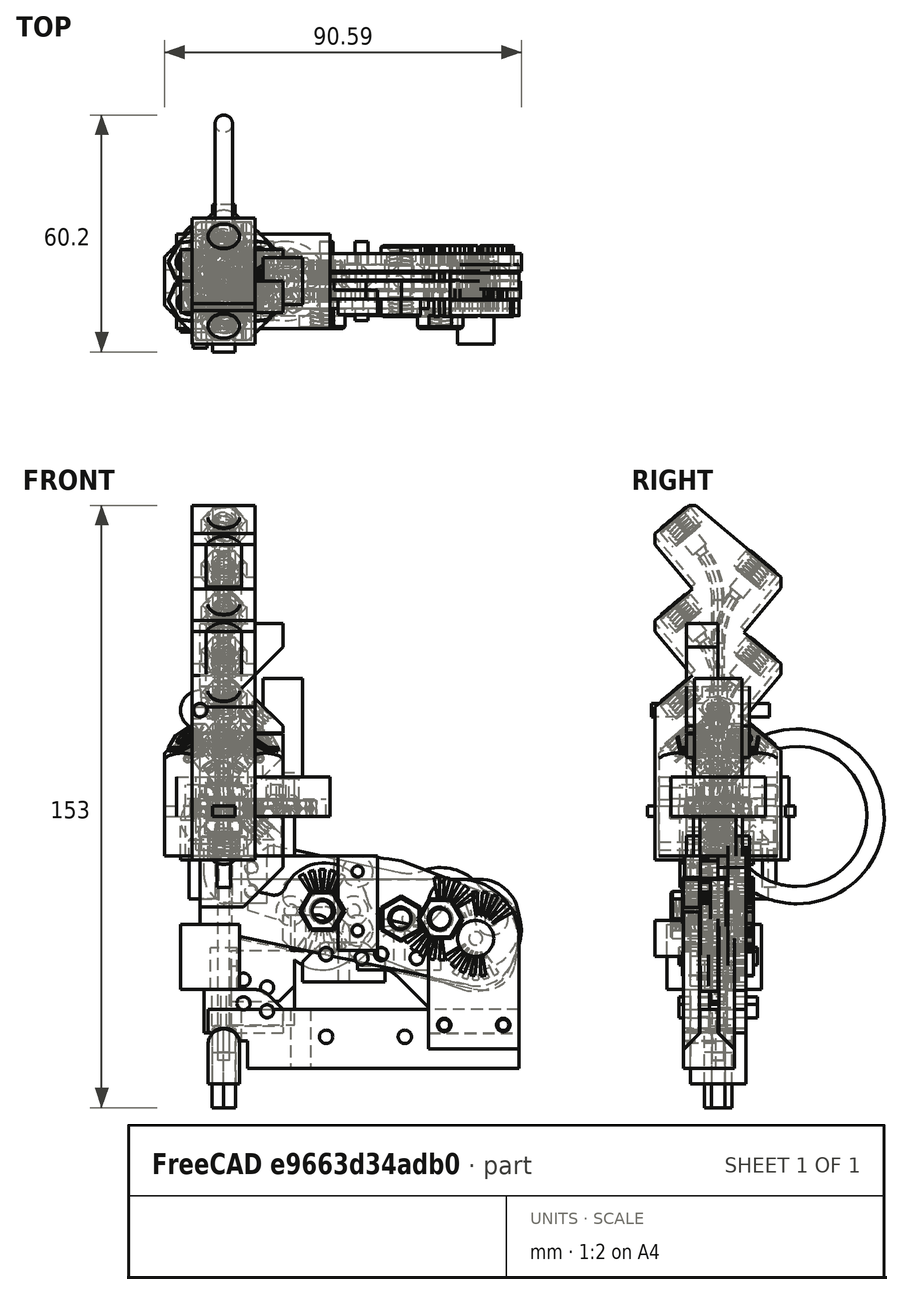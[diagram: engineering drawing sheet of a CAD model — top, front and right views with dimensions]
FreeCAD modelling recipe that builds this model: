
FCSTD DOCUMENT  (FreeCAD 0.17R13528 (Git))
Label: guillotine-old
License: All rights reserved
LicenseURL: http://en.wikipedia.org/wiki/All_rights_reserved
objects: Part::Cylinder×189, Part::Box×143, Part::Cut×137, Part::MultiFuse×132, Part::MultiCommon×72, Part::Feature×58, Part::Cone×39, Part::Fillet×29, Part::Chamfer×26, Part::Mirroring×13, Part::Torus×9, App::DocumentObjectGroup×5, Part::Fuse×2, Part::Sphere×1
note: 850 computed .brp shape members not serialized (recipe doc carries the construction recipe); baked Part::Feature solids carry a one-line shape summary decoded from their .brp

FEATURE [Part::Feature] Part__Feature027  label="1310"
  Placement = pos=(2,0,0) rot=(0,0,1;0rad)
  shape: bbox 13.32 x 18 x 18 mm, 178 faces (baked)
FEATURE [Part::Box] Box  label="Cube"
  AttacherType = Attacher::AttachEngine3D
  Height = 20
  Length = 4
  Placement = pos=(0,-10,-10) rot=(0,0,1;0rad)
  Width = 20
FEATURE [Part::Cylinder] Cylinder
  Angle = 360
  AttacherType = Attacher::AttachEngine3D
  Height = 25
  Placement = pos=(-4,0,0) rot=(0,1,0;1.5708rad)
  Radius = 5
FEATURE [Part::MultiFuse] Fusion
  Shapes = -> [Part__Feature027,Cylinder]
FEATURE [Part::MultiCommon] Common  label="gear-blank"
  Shapes = -> [Fusion,Box]
FEATURE [Part::Cylinder] Cylinder001
  Angle = 360
  AttacherType = Attacher::AttachEngine3D
  Height = 10
  Placement = pos=(-2,0,0) rot=(0,1,0;1.5708rad)
  Radius = 1.7
FEATURE [Part::Feature] Part__Feature028  label="1310001"
  Placement = pos=(2,0,0) rot=(0,0,1;0rad)
  shape: bbox 13.32 x 18 x 18 mm, 178 faces (baked)
FEATURE [Part::Box] Box001  label="Cube001"
  AttacherType = Attacher::AttachEngine3D
  Height = 20
  Length = 4
  Placement = pos=(0,-10,-10) rot=(0,0,1;0rad)
  Width = 20
FEATURE [Part::Cylinder] Cylinder002
  Angle = 360
  AttacherType = Attacher::AttachEngine3D
  Height = 25
  Placement = pos=(-4,0,0) rot=(0,1,0;1.5708rad)
  Radius = 5
FEATURE [Part::MultiFuse] Fusion001
  Shapes = -> [Part__Feature028,Cylinder002]
FEATURE [Part::MultiCommon] Common001  label="gear-blank001"
  Shapes = -> [Fusion001,Box001]
FEATURE [Part::Cylinder] Cylinder003
  Angle = 360
  AttacherType = Attacher::AttachEngine3D
  Height = 10
  Placement = pos=(-2,0,0) rot=(0,1,0;1.5708rad)
  Radius = 1.8
FEATURE [Part::Cut] Cut  label="shaft-gear-a"
  Base = -> Common
  Placement = pos=(0,0,0) rot=(0,-1,0;1.5708rad)
  Tool = -> Cylinder001
FEATURE [Part::Box] Box002  label="Cube002"
  AttacherType = Attacher::AttachEngine3D
  Height = 10
  Length = 15
  Placement = pos=(-4,-6,1) rot=(0,0,1;0rad)
  Width = 10
FEATURE [Part::Cut] Cut001
  Base = -> Cylinder003
  Tool = -> Box002
FEATURE [Part::Cut] Cut002  label="motor-gear"
  Base = -> Common001
  Placement = pos=(15,0,4) rot=(0,1,0;1.5708rad)
  Tool = -> Cut001
FEATURE [Part::Fuse] Fusion003
FEATURE [Part::Cylinder] Cylinder012
  Angle = 360
  AttacherType = Attacher::AttachEngine3D
  Height = 10
  Placement = pos=(5,-4.5,0) rot=(0,1,0;1.5708rad)
  Radius = 0.8
FEATURE [Part::Fuse] Fusion048  label="motor"
  Base = -> Cylinder012
  Placement = pos=(15,0,0) rot=(0,-1,0;1.5708rad)
  Tool = -> Fusion003
FEATURE [Part::Feature] Part__Feature035  label="423001001"
  Placement = pos=(0,0,-2) rot=(0,0,1;3.74342rad)
  shape: bbox 9 x 9 x 4 mm, 22 faces (baked)
FEATURE [Part::Feature] Part__Feature066  label="212001001001"
  Placement = pos=(0,0,0) rot=(0.905883,0.423527,0;3.14159rad)
  shape: bbox 7 x 7 x 0.5 mm, 6 faces (baked)
FEATURE [Part::Cylinder] Cylinder013
  Angle = 360
  AttacherType = Attacher::AttachEngine3D
  Height = 74
  Placement = pos=(0,0,-62) rot=(0,0,1;0rad)
  Radius = 1.5
FEATURE [Part::Cylinder] Cylinder014
  Angle = 360
  AttacherType = Attacher::AttachEngine3D
  Height = 8
  Placement = pos=(0,0,1) rot=(0,0,1;0rad)
  Radius = 4
FEATURE [Part::Box] Box003  label="Cube003"
  AttacherType = Attacher::AttachEngine3D
  Height = 10
  Length = 10
  Placement = pos=(-12.85,-5,0) rot=(0,0,1;0rad)
  Width = 10
FEATURE [Part::Feature] Box001001
  Placement = pos=(-2.09487,-13.6284,0) rot=(0,0,1;1.0472rad)
  shape: bbox 13.66 x 13.66 x 10 mm, 6 faces (baked)
FEATURE [Part::Feature] Box001002
  Placement = pos=(10.7551,-8.62843,0) rot=(0,0,1;2.0944rad)
  shape: bbox 13.66 x 13.66 x 10 mm, 6 faces (baked)
FEATURE [Part::Feature] Box001003
  Placement = pos=(12.85,5,0) rot=(0,0,1;3.14159rad)
  shape: bbox 10 x 10 x 10 mm, 6 faces (baked)
FEATURE [Part::Feature] Box001004
  Placement = pos=(2.09487,13.6284,0) rot=(0,0,1;4.18879rad)
  shape: bbox 13.66 x 13.66 x 10 mm, 6 faces (baked)
FEATURE [Part::Feature] Box001005
  Placement = pos=(-10.7551,8.62843,0) rot=(0,0,-1;1.0472rad)
  shape: bbox 13.66 x 13.66 x 10 mm, 6 faces (baked)
FEATURE [Part::MultiFuse] Fusion049
  Shapes = -> [Box003,Box001005,Box001001,Box001002,Box001003,Box001004]
FEATURE [Part::Cut] Cut003  label="m3-nut"
  Base = -> Cylinder014
  Placement = pos=(0,0,1) rot=(0,0,1;0rad)
  Tool = -> Fusion049
FEATURE [Part::Feature] Part__Feature067  label="423001001001"
  Placement = pos=(0,0,7) rot=(0,0,1;3.74342rad)
  shape: bbox 9 x 9 x 4 mm, 22 faces (baked)
FEATURE [Part::Cylinder] Cylinder015
  Angle = 360
  AttacherType = Attacher::AttachEngine3D
  Height = 100
  Placement = pos=(0,0,-12) rot=(0,0,1;0rad)
  Radius = 1.7
FEATURE [Part::MultiFuse] Fusion050
  Shapes = -> [Cylinder015,Cut003]
FEATURE [Part::Cut] Cut004  label="shaft-gear"
  Base = -> Cut
  Tool = -> Fusion050
FEATURE [Part::Box] Box001006  label="Cube004"
  AttacherType = Attacher::AttachEngine3D
  Height = 10
  Length = 39
  Placement = pos=(-12,-12,0) rot=(0,0,1;0rad)
  Width = 24
FEATURE [Part::Cylinder] Cylinder016
  Angle = 360
  AttacherType = Attacher::AttachEngine3D
  Height = 30
  Placement = pos=(0,0,-12) rot=(0,0,1;0rad)
  Radius = 3.5
FEATURE [Part::Cylinder] Cylinder017
  Angle = 360
  AttacherType = Attacher::AttachEngine3D
  Height = 30
  Placement = pos=(0,0,-21.5) rot=(0,0,1;0rad)
  Radius = 4.7
FEATURE [Part::Cylinder] Cylinder018
  Angle = 360
  AttacherType = Attacher::AttachEngine3D
  Height = 30
  Placement = pos=(0,0,-25.5) rot=(0,0,1;0rad)
  Radius = 10
FEATURE [Part::Cylinder] Cylinder019
  Angle = 360
  AttacherType = Attacher::AttachEngine3D
  Height = 30
  Placement = pos=(16,0,-25.5) rot=(0,0,1;0rad)
  Radius = 10
FEATURE [Part::Cylinder] Cylinder020
  Angle = 360
  AttacherType = Attacher::AttachEngine3D
  Height = 30
  Placement = pos=(17,0,-12.5) rot=(0,0,1;0rad)
  Radius = 2.1
FEATURE [Part::Cylinder] Cylinder021
  Angle = 360
  AttacherType = Attacher::AttachEngine3D
  Height = 30
  Placement = pos=(17,-4.5,-12.5) rot=(0,0,1;0rad)
  Radius = 1
FEATURE [Part::Cylinder] Cylinder022
  Angle = 360
  AttacherType = Attacher::AttachEngine3D
  Height = 30
  Placement = pos=(17,4.5,-12.5) rot=(0,0,1;0rad)
  Radius = 1
FEATURE [Part::Cylinder] Cylinder023
  Angle = 360
  AttacherType = Attacher::AttachEngine3D
  Height = 30
  Placement = pos=(13,0,-12.5) rot=(0,0,1;0rad)
  Radius = 2.1
FEATURE [Part::Cylinder] Cylinder024
  Angle = 360
  AttacherType = Attacher::AttachEngine3D
  Height = 30
  Placement = pos=(13,-4.5,-12.5) rot=(0,0,1;0rad)
  Radius = 1
FEATURE [Part::Cylinder] Cylinder025
  Angle = 360
  AttacherType = Attacher::AttachEngine3D
  Height = 30
  Placement = pos=(13,4.5,-12.5) rot=(0,0,1;0rad)
  Radius = 1
FEATURE [Part::Box] Box001007  label="Cube005"
  AttacherType = Attacher::AttachEngine3D
  Height = 27
  Length = 4
  Placement = pos=(13,-2.1,-11) rot=(0,0,1;0rad)
  Width = 4.2
FEATURE [Part::Box] Box001008  label="Cube006"
  AttacherType = Attacher::AttachEngine3D
  Height = 27
  Length = 4
  Placement = pos=(13,-5.5,-11) rot=(0,0,1;0rad)
  Width = 2
FEATURE [Part::Box] Box001009  label="Cube007"
  AttacherType = Attacher::AttachEngine3D
  Height = 27
  Length = 4
  Placement = pos=(13,3.5,-11) rot=(0,0,1;0rad)
  Width = 2
FEATURE [Part::MultiFuse] Fusion052  label="motor-slots"
  Shapes = -> [Box001009,Cylinder021,Cylinder022,Box001007,Cylinder020,Cylinder023,Cylinder024,Box001008,Cylinder025]
FEATURE [Part::Cylinder] Cylinder026
  Angle = 360
  AttacherType = Attacher::AttachEngine3D
  Height = 30
  Placement = pos=(15,0,-25.5) rot=(0,0,1;0rad)
  Radius = 10
FEATURE [Part::MultiFuse] Fusion053  label="gearbox-cavity-1"
  Shapes = -> [Cylinder019,Cylinder016,Cylinder017,Cylinder018,Cylinder026]
FEATURE [Part::MultiFuse] Fusion054  label="gearbox-cavity-2"
  Shapes = -> [Fusion053,Fusion052]
FEATURE [Part::Cut] Cut005  label="gearbox-1"
  Base = -> Box001006
  Tool = -> Fusion054
FEATURE [Part::Chamfer] Chamfer  label="gearbox-2"
  Base = -> Cut005
  Edges = 10 edges r=1: [Edge47,Edge50,Edge52,Edge54,Edge55,Edge58,Edge60,Edge62,Edge64,Edge65]
FEATURE [Part::Box] Box001010  label="Cube008"
  AttacherType = Attacher::AttachEngine3D
  Height = 8
  Length = 14
  Placement = pos=(-7,-15,-8.5) rot=(0,0,1;0rad)
  Width = 30
FEATURE [Part::Box] Box001011  label="Cube009"
  AttacherType = Attacher::AttachEngine3D
  Height = 11
  Length = 14
  Placement = pos=(-7,-15,-1) rot=(0,0,1;0rad)
  Width = 2.8
FEATURE [Part::Box] Box001012  label="Cube010"
  AttacherType = Attacher::AttachEngine3D
  Height = 11
  Length = 14
  Placement = pos=(-7,12.2,-1) rot=(0,0,1;0rad)
  Width = 2.8
FEATURE [Part::MultiFuse] Fusion055  label="bearing-clamp-1"
  Shapes = -> [Box001010,Box001012,Box001011]
FEATURE [Part::Cylinder] Cylinder027  label="M3-tap-1"
  Angle = 360
  AttacherType = Attacher::AttachEngine3D
  Height = 19
  Placement = pos=(-4,24,6) rot=(1,0,0;1.5708rad)
  Radius = 1.4
FEATURE [Part::Cylinder] Cylinder028  label="M3-tap-2"
  Angle = 360
  AttacherType = Attacher::AttachEngine3D
  Height = 19
  Placement = pos=(4,24,6) rot=(1,0,0;1.5708rad)
  Radius = 1.4
FEATURE [Part::Cylinder] Cylinder029  label="M3-clear-1"
  Angle = 360
  AttacherType = Attacher::AttachEngine3D
  Height = 19
  Placement = pos=(-4,24,6) rot=(1,0,0;1.5708rad)
  Radius = 1.7
FEATURE [Part::Cylinder] Cylinder030  label="M3-clear-2"
  Angle = 360
  AttacherType = Attacher::AttachEngine3D
  Height = 19
  Placement = pos=(4,24,6) rot=(1,0,0;1.5708rad)
  Radius = 1.7
FEATURE [Part::Cylinder] Cylinder031  label="M3-tap-003"
  Angle = 360
  AttacherType = Attacher::AttachEngine3D
  Height = 19
  Placement = pos=(-4,24,6) rot=(1,0,0;1.5708rad)
  Radius = 1.4
FEATURE [Part::Cylinder] Cylinder032  label="M3-tap-004"
  Angle = 360
  AttacherType = Attacher::AttachEngine3D
  Height = 19
  Placement = pos=(4,24,6) rot=(1,0,0;1.5708rad)
  Radius = 1.4
FEATURE [Part::Cylinder] Cylinder033  label="M3-clear-003"
  Angle = 360
  AttacherType = Attacher::AttachEngine3D
  Height = 19
  Placement = pos=(4,24,6) rot=(1,0,0;1.5708rad)
  Radius = 1.7
FEATURE [Part::Cylinder] Cylinder034  label="M3-clear-004"
  Angle = 360
  AttacherType = Attacher::AttachEngine3D
  Height = 19
  Placement = pos=(-4,24,6) rot=(1,0,0;1.5708rad)
  Radius = 1.7
FEATURE [Part::Mirroring] Part__Mirroring  label="M3-tap-003 (Mirror #1)"
  Base = (0,0,0)
  Normal = (0,1,0)
  Source = -> Cylinder031
FEATURE [Part::Mirroring] Part__Mirroring001  label="M3-tap-004 (Mirror #2)"
  Base = (0,0,0)
  Normal = (0,1,0)
  Source = -> Cylinder032
FEATURE [Part::Mirroring] Part__Mirroring002  label="M3-clear-003 (Mirror #3)"
  Base = (0,0,0)
  Normal = (0,1,0)
  Source = -> Cylinder033
FEATURE [Part::Mirroring] Part__Mirroring003  label="M3-clear-004 (Mirror #4)"
  Base = (0,0,0)
  Normal = (0,1,0)
  Source = -> Cylinder034
FEATURE [Part::MultiFuse] Fusion056  label="M3-tap-a"
  Shapes = -> [Cylinder027,Cylinder028,Part__Mirroring,Part__Mirroring001]
FEATURE [Part::MultiFuse] Fusion057  label="M3-clear-a"
  Shapes = -> [Cylinder029,Cylinder030,Part__Mirroring002,Part__Mirroring003]
FEATURE [Part::Cut] Cut006  label="bearing-clamp-2"
  Base = -> Fusion055
  Tool = -> Fusion057
FEATURE [Part::Cut] Cut007  label="gearbox-3"
  Base = -> Chamfer
  Tool = -> Fusion056
FEATURE [Part::Cylinder] Cylinder035
  Angle = 360
  AttacherType = Attacher::AttachEngine3D
  Height = 30
  Placement = pos=(0,0,-4.5) rot=(0,0,1;0rad)
  Radius = 4.7
FEATURE [Part::Cylinder] Cylinder036
  Angle = 360
  AttacherType = Attacher::AttachEngine3D
  Height = 30
  Placement = pos=(0,0,-9) rot=(0,0,1;0rad)
  Radius = 3.5
FEATURE [Part::Box] Box001013  label="Cube011"
  AttacherType = Attacher::AttachEngine3D
  Height = 12
  Length = 80
  Placement = pos=(0,-2,0) rot=(0,0,1;0rad)
  Width = 4
FEATURE [Part::Cylinder] Cylinder037
  Angle = 360
  AttacherType = Attacher::AttachEngine3D
  Height = 4
  Placement = pos=(11,2,12) rot=(1,0,0;1.5708rad)
  Radius = 11
FEATURE [Part::Cylinder] Cylinder038
  Angle = 360
  AttacherType = Attacher::AttachEngine3D
  Height = 4
  Placement = pos=(50,2,12) rot=(1,0,0;1.5708rad)
  Radius = 11
FEATURE [Part::MultiFuse] Fusion059
  Shapes = -> [Box001013,Cylinder037,Cylinder038]
FEATURE [Part::Fillet] Fillet
  Base = -> Fusion059
  Edges = 1 edges r=7: [Edge21]
FEATURE [Part::Fillet] Fillet001
  Base = -> Fillet
  Edges = 2 edges r=7: [Edge12,Edge20]
FEATURE [Part::Cylinder] Cylinder039
  Angle = 360
  AttacherType = Attacher::AttachEngine3D
  Height = 10
  Placement = pos=(50,5,8) rot=(1,0,0;1.5708rad)
  Radius = 3.2
FEATURE [Part::Cut] Cut009
  Base = -> Fillet001
  Tool = -> Cylinder039
FEATURE [Part::Box] Box001014  label="Cube012"
  AttacherType = Attacher::AttachEngine3D
  Height = 13
  Length = 2
  Placement = pos=(0,-5,0) rot=(0,0,1;0rad)
  Width = 10
FEATURE [Part::Box] Box001015  label="Cube013"
  AttacherType = Attacher::AttachEngine3D
  Height = 2
  Length = 13
  Placement = pos=(0,-5,0) rot=(0,-1,0;1.39626rad)
  Width = 10
FEATURE [Part::Cylinder] Cylinder040
  Angle = 360
  AttacherType = Attacher::AttachEngine3D
  Height = 13
  Placement = pos=(0,7,0) rot=(1,0,0;1.5708rad)
  Radius = 2
FEATURE [Part::Cylinder] Cylinder041
  Angle = 360
  AttacherType = Attacher::AttachEngine3D
  Height = 8
  Placement = pos=(0,4,0) rot=(1,0,0;1.5708rad)
  Radius = 8
FEATURE [Part::Cut] Cut010
  Base = -> Cylinder041
  Tool = -> Cylinder040
FEATURE [Part::MultiCommon] Common002
  Shapes = -> [Box001014,Box001015]
FEATURE [Part::MultiCommon] Common003
  Placement = pos=(50,0,11) rot=(0,-1,0;0.087266rad)
  Shapes = -> [Cut010,Common002]
FEATURE [Part::MultiCommon] Common004
  Placement = pos=(50.7765,0,10.8978) rot=(0,1,0;0.174533rad)
  Shapes = -> [Cut010,Common002]
FEATURE [Part::MultiCommon] Common005
  Placement = pos=(49.2235,0,10.8978) rot=(0,-1,0;0.349066rad)
  Shapes = -> [Cut010,Common002]
FEATURE [Part::MultiCommon] Common006
  Placement = pos=(51.5,0,10.5981) rot=(0,1,0;0.436332rad)
  Shapes = -> [Cut010,Common002]
FEATURE [Part::MultiCommon] Common007
  Placement = pos=(48.5,0,10.5981) rot=(0,-1,0;0.610865rad)
  Shapes = -> [Cut010,Common002]
FEATURE [Part::MultiFuse] Fusion060  label="strength-slots"
  Shapes = -> [Common003,Common006,Common005,Common004,Common007]
FEATURE [Part::MultiFuse] Fusion061  label="strength-slots001"
  Placement = pos=(61,0,22) rot=(0,1,0;3.14159rad)
  Shapes = -> [Common003,Common006,Common005,Common004,Common007]
FEATURE [Part::Cut] Cut011
  Base = -> Cut009
  Tool = -> Fusion060
FEATURE [Part::Cylinder] Cylinder042
  Angle = 360
  AttacherType = Attacher::AttachEngine3D
  Height = 10
  Placement = pos=(11,5,15) rot=(1,0,0;1.5708rad)
  Radius = 4.6
FEATURE [Part::Cut] Cut012
  Base = -> Cut011
  Tool = -> Cylinder042
FEATURE [Part::Cut] Cut013
  Base = -> Cut012
  Tool = -> Fusion061
FEATURE [Part::Fillet] Fillet002  label="cutting-lever-1"
  Base = -> Cut013
  Edges = 1 edges r=10: [Edge73]
  Placement = pos=(75,0,-16) rot=(0,1,0;3.14159rad)
FEATURE [Part::Box] Box001016  label="Cube014"
  AttacherType = Attacher::AttachEngine3D
  Height = 12
  Length = 80
  Placement = pos=(0,-7,12) rot=(0,0,1;0rad)
  Width = 14
FEATURE [Part::Cylinder] Cylinder043
  Angle = 360
  AttacherType = Attacher::AttachEngine3D
  Height = 14
  Placement = pos=(11,7,12) rot=(1,0,0;1.5708rad)
  Radius = 11
FEATURE [Part::Cylinder] Cylinder044
  Angle = 360
  AttacherType = Attacher::AttachEngine3D
  Height = 14
  Placement = pos=(50,7,12) rot=(1,0,0;1.5708rad)
  Radius = 11
FEATURE [Part::MultiFuse] Fusion062  label="cutting-holder-1"
  Shapes = -> [Cylinder044,Cylinder043,Box001016]
FEATURE [Part::Fillet] Fillet003
  Base = -> Fusion062
  Edges = 1 edges r=10: [Edge1]
  Placement = pos=(-1.94863,0,5.46002) rot=(0,1,0;0.20944rad)
FEATURE [Part::Cylinder] Cylinder045
  Angle = 360
  AttacherType = Attacher::AttachEngine3D
  Height = 20
  Placement = pos=(11,10,15) rot=(1,0,0;1.5708rad)
  Radius = 1.7
FEATURE [Part::Cylinder] Cylinder046
  Angle = 360
  AttacherType = Attacher::AttachEngine3D
  Height = 20
  Placement = pos=(50,10,8) rot=(1,0,0;1.5708rad)
  Radius = 3.2
FEATURE [Part::Box] Box001017  label="Cube015"
  AttacherType = Attacher::AttachEngine3D
  Height = 2
  Length = 13
  Placement = pos=(0,-10,0) rot=(0,-1,0;1.39626rad)
  Width = 20
FEATURE [Part::Box] Box001018  label="Cube016"
  AttacherType = Attacher::AttachEngine3D
  Height = 13
  Length = 2
  Placement = pos=(0,-10,0) rot=(0,0,1;0rad)
  Width = 20
FEATURE [Part::Cylinder] Cylinder047
  Angle = 360
  AttacherType = Attacher::AttachEngine3D
  Height = 26
  Placement = pos=(0,12,0) rot=(1,0,0;1.5708rad)
  Radius = 2
FEATURE [Part::Cylinder] Cylinder048
  Angle = 360
  AttacherType = Attacher::AttachEngine3D
  Height = 18
  Placement = pos=(0,9,0) rot=(1,0,0;1.5708rad)
  Radius = 8
FEATURE [Part::Cut] Cut014
  Base = -> Cylinder048
  Tool = -> Cylinder047
FEATURE [Part::MultiCommon] Common012  label="strength-slot-005"
  Placement = pos=(0,0,2.5) rot=(0,-1,0;0.087266rad)
  Shapes = -> [Box001017,Box001018,Cut014]
FEATURE [Part::Box] Box001019  label="Cube017"
  AttacherType = Attacher::AttachEngine3D
  Height = 40
  Length = 100
  Placement = pos=(-2,-2.5,-8) rot=(0,0,1;0rad)
  Width = 22
FEATURE [Part::MultiCommon] Common013  label="strength-slot-006"
  Placement = pos=(0.647048,0,2.41481) rot=(0,1,0;0.174533rad)
  Shapes = -> [Box001017,Box001018,Cut014]
FEATURE [Part::MultiCommon] Common014  label="strength-slot-007"
  Placement = pos=(1.25,0,2.16506) rot=(0,1,0;0.436332rad)
  Shapes = -> [Box001017,Box001018,Cut014]
FEATURE [Part::MultiCommon] Common015  label="strength-slot-008"
  Placement = pos=(-0.647048,0,2.41481) rot=(0,-1,0;0.349066rad)
  Shapes = -> [Box001017,Box001018,Cut014]
FEATURE [Part::MultiCommon] Common016  label="strength-slot-009"
  Placement = pos=(-1.25,0,2.16506) rot=(0,-1,0;0.610865rad)
  Shapes = -> [Box001017,Box001018,Cut014]
FEATURE [Part::MultiFuse] Fusion063  label="strength-slots002"
  Placement = pos=(11,0,15) rot=(0,0,1;0rad)
  Shapes = -> [Common012,Common013,Common014,Common015,Common016]
FEATURE [Part::MultiFuse] Fusion064  label="strength-slots003"
  Placement = pos=(50,0,8) rot=(0,1,0;3.14159rad)
  Shapes = -> [Common012,Common013,Common014,Common015,Common016]
FEATURE [Part::MultiFuse] Fusion065
  Shapes = -> [Cylinder045,Cylinder046,Fusion063,Fusion064]
FEATURE [Part::Box] Box001020  label="Cube018"
  AttacherType = Attacher::AttachEngine3D
  Height = 10
  Length = 21
  Placement = pos=(20,-2.5,13) rot=(0,0,1;0rad)
  Width = 9.5
FEATURE [Part::Chamfer] Chamfer001
  Base = -> Box001020
  Edges = 2 edges r=8: [Edge4,Edge8]
FEATURE [Part::Fillet] Fillet004
  Base = -> Chamfer001
  Edges = 2 edges r=2: [Edge10,Edge17]
FEATURE [Part::Fillet] Fillet005
  Base = -> Fillet003
  Edges = 1 edges r=7: [Edge26]
FEATURE [Part::Fillet] Fillet006
  Base = -> Fillet005
  Edges = 1 edges r=7: [Edge11]
FEATURE [Part::Cut] Cut015
  Base = -> Fillet006
  Tool = -> Fusion065
FEATURE [Part::Cut] Cut016  label="cutting-holder-2"
  Base = -> Cut015
  Tool = -> Box001019
FEATURE [Part::Cut] Cut017  label="cutting-holder-003"
  Base = -> Cut015
  Tool = -> Box001019
FEATURE [Part::Mirroring] Part__Mirroring004  label="cutting-holder-004"
  Base = (0,0,0)
  Normal = (0,1,0)
  Source = -> Cut017
FEATURE [Part::MultiFuse] Fusion066  label="cutting-holder-base"
  Shapes = -> [Fillet004,Part__Mirroring004]
FEATURE [Part::Cylinder] Cylinder049
  Angle = 360
  AttacherType = Attacher::AttachEngine3D
  Height = 30
  Placement = pos=(30.5,0,0) rot=(0,0,1;0rad)
  Radius = 1.4
FEATURE [Part::Cut] Cut018  label="cutting-holder-base-2"
  Base = -> Fusion066
  Tool = -> Cylinder049
FEATURE [Part::Cylinder] Cylinder050
  Angle = 360
  AttacherType = Attacher::AttachEngine3D
  Height = 20
  Placement = pos=(26,10,20) rot=(1,0,0;1.5708rad)
  Radius = 1.7
FEATURE [Part::Cylinder] Cylinder051
  Angle = 360
  AttacherType = Attacher::AttachEngine3D
  Height = 20
  Placement = pos=(35,10,19) rot=(1,0,0;1.5708rad)
  Radius = 1.7
FEATURE [Part::Cylinder] Cylinder052
  Angle = 360
  AttacherType = Attacher::AttachEngine3D
  Height = 20
  Placement = pos=(26,10,20) rot=(1,0,0;1.5708rad)
  Radius = 1.4
FEATURE [Part::Cylinder] Cylinder053
  Angle = 360
  AttacherType = Attacher::AttachEngine3D
  Height = 20
  Placement = pos=(35,10,19) rot=(1,0,0;1.5708rad)
  Radius = 1.4
FEATURE [Part::MultiFuse] Fusion067
  Shapes = -> [Cylinder050,Cylinder051]
FEATURE [Part::MultiFuse] Fusion068
  Shapes = -> [Cylinder052,Cylinder053]
FEATURE [Part::Cut] Cut019  label="cut-holder-4"
  Base = -> Cut016
  Tool = -> Fusion067
FEATURE [Part::Cut] Cut020  label="cut-holder-base-3"
  Base = -> Cut018
  Placement = pos=(75,0,-16) rot=(0,1,0;3.14159rad)
  Tool = -> Fusion068
FEATURE [Part::Feature] Part__Feature055  label="M6 thread"
  Placement = pos=(50,-7,8) rot=(1,0,0;1.5708rad)
  shape: bbox 11.55 x 5.798 x 10 mm, 23 faces (baked)
FEATURE [Part::MultiFuse] Fusion069  label="cut-holder-5"
  Placement = pos=(75,0,-16) rot=(0,1,0;3.14159rad)
  Shapes = -> [Cut019,Part__Feature055]
FEATURE [Part::Box] Box001021  label="Cube019"
  AttacherType = Attacher::AttachEngine3D
  Height = 19
  Length = 16
  Placement = pos=(2,-2,-47) rot=(0,0,1;0rad)
  Width = 4
FEATURE [Part::Box] Box001022  label="Cube020"
  AttacherType = Attacher::AttachEngine3D
  Height = 11
  Length = 23
  Placement = pos=(-5,-7,-42) rot=(0,0,1;0rad)
  Width = 14
FEATURE [Part::Box] Box001023  label="Cube021"
  AttacherType = Attacher::AttachEngine3D
  Height = 22
  Length = 14
  Placement = pos=(-12,-4,-33) rot=(0,0,1;0rad)
  Width = 9
FEATURE [Part::Cut] Cut021
  Base = -> Fillet002
  Tool = -> Box001023
FEATURE [Part::Box] Box001024  label="Cube022"
  AttacherType = Attacher::AttachEngine3D
  Height = 13
  Length = 23
  Placement = pos=(-3,-2.2,-47.2) rot=(0,0,1;0rad)
  Width = 4.4
FEATURE [Part::Chamfer] Chamfer002
  Base = -> Box001021
  Edges = 1 edges r=4: [Edge8]
FEATURE [Part::Chamfer] Chamfer003
  Base = -> Box001022
  Edges = 1 edges r=8: [Edge6]
FEATURE [Part::Fillet] Fillet007
  Base = -> Chamfer003
  Edges = 1 edges r=5: [Edge9]
FEATURE [Part::Box] Box001025  label="Cube023"
  AttacherType = Attacher::AttachEngine3D
  Height = 10
  Length = 10
  Placement = pos=(15,-13,-44) rot=(0,0,1;0rad)
  Width = 27
FEATURE [Part::Cut] Cut022
  Base = -> Fillet007
  Placement = pos=(0,0,-7) rot=(0,0,1;0rad)
  Tool = -> Box001025
FEATURE [Part::Cylinder] Cylinder054
  Angle = 360
  AttacherType = Attacher::AttachEngine3D
  Height = 20
  Placement = pos=(11,10,-43.5) rot=(1,0,0;1.5708rad)
  Radius = 1.7
FEATURE [Part::Cylinder] Cylinder055
  Angle = 360
  AttacherType = Attacher::AttachEngine3D
  Height = 20
  Placement = pos=(5,10,-41.5) rot=(1,0,0;1.5708rad)
  Radius = 1.7
FEATURE [Part::Cylinder] Cylinder056
  Angle = 360
  AttacherType = Attacher::AttachEngine3D
  Height = 20
  Placement = pos=(11,19,-43.5) rot=(1,0,0;1.5708rad)
  Radius = 1.7
FEATURE [Part::Cylinder] Cylinder057
  Angle = 360
  AttacherType = Attacher::AttachEngine3D
  Height = 20
  Placement = pos=(5,19,-41.5) rot=(1,0,0;1.5708rad)
  Radius = 1.7
FEATURE [Part::Cylinder] Cylinder058
  Angle = 360
  AttacherType = Attacher::AttachEngine3D
  Height = 20
  Placement = pos=(11,-1,-43.5) rot=(1,0,0;1.5708rad)
  Radius = 1.4
FEATURE [Part::Cylinder] Cylinder059
  Angle = 360
  AttacherType = Attacher::AttachEngine3D
  Height = 20
  Placement = pos=(5,-1,-41.5) rot=(1,0,0;1.5708rad)
  Radius = 1.4
FEATURE [Part::Cylinder] Cylinder060
  Angle = 360
  AttacherType = Attacher::AttachEngine3D
  Height = 62
  Placement = pos=(0,0,-56) rot=(0,0,1;0rad)
  Radius = 2.3
FEATURE [Part::Cylinder] Cylinder061  label="rocker-1"
  Angle = 360
  AttacherType = Attacher::AttachEngine3D
  Height = 14
  Placement = pos=(0,7,-52) rot=(1,0,0;1.5708rad)
  Radius = 4
FEATURE [Part::Cylinder] Cylinder062
  Angle = 360
  AttacherType = Attacher::AttachEngine3D
  Height = 24
  Placement = pos=(0,11,-52) rot=(1,0,0;1.5708rad)
  Radius = 4.2
FEATURE [Part::MultiFuse] Fusion074
  Shapes = -> [Cylinder058,Cylinder056,Cylinder057,Cylinder059]
FEATURE [Part::Cut] Cut027
  Base = -> Cut022
  Tool = -> Fusion074
FEATURE [Part::Cut] Cut028
  Base = -> Cut027
  Tool = -> Box001024
FEATURE [Part::Cut] Cut029
  Base = -> Cut028
  Tool = -> Cylinder062
FEATURE [Part::MultiFuse] Fusion075
  Shapes = -> [Cylinder054,Cylinder055]
FEATURE [Part::Cut] Cut031
  Base = -> Chamfer002
  Tool = -> Fusion075
FEATURE [Part::MultiFuse] Fusion076  label="cut-lever-7"
  Shapes = -> [Cut021,Cut031]
FEATURE [Part::Box] Box001026  label="Cube024"
  AttacherType = Attacher::AttachEngine3D
  Height = 10
  Length = 8
  Placement = pos=(-4,-7,-62) rot=(0,0,1;0rad)
  Width = 14
FEATURE [Part::MultiFuse] Fusion077  label="rocker-2"
  Shapes = -> [Cylinder061,Box001026]
FEATURE [Part::Cylinder] Cylinder063
  Angle = 360
  AttacherType = Attacher::AttachEngine3D
  Height = 62
  Placement = pos=(0,0,-75) rot=(0,0,1;0rad)
  Radius = 1.5
FEATURE [Part::Cut] Cut032  label="rocker-3"
  Base = -> Fusion077
  Tool = -> Cylinder063
FEATURE [Part::Cylinder] Cylinder064
  Angle = 360
  AttacherType = Attacher::AttachEngine3D
  Height = 20
  Placement = pos=(0,0,-74) rot=(0,0,1;0rad)
  Radius = 4
FEATURE [Part::Box] Box001027  label="Cube025"
  AttacherType = Attacher::AttachEngine3D
  Height = 25
  Length = 10
  Placement = pos=(3,-5,-77) rot=(0,0,1;0rad)
  Width = 10
FEATURE [Part::Cylinder] Cylinder065
  Angle = 360
  AttacherType = Attacher::AttachEngine3D
  Height = 62
  Placement = pos=(0,0,-59) rot=(0,0,1;0rad)
  Radius = 2
FEATURE [Part::Cylinder] Cylinder066  label="rocker-005"
  Angle = 360
  AttacherType = Attacher::AttachEngine3D
  Height = 14
  Placement = pos=(0,7,-8) rot=(1,0,0;1.5708rad)
  Radius = 4
FEATURE [Part::MultiFuse] Fusion080  label="bearing-nut"
  Shapes = -> [Cylinder035,Cylinder036]
FEATURE [Part::Cut] Cut035
  Base = -> Cylinder066
  Tool = -> Cylinder065
FEATURE [Part::MultiFuse] Fusion081
  Shapes = -> [Cut006,Cut035]
FEATURE [Part::Cut] Cut036  label="bearing-clamp-003"
  Base = -> Fusion081
  Tool = -> Fusion080
FEATURE [Part::Cylinder] Cylinder067  label="rocker-006"
  Angle = 360
  AttacherType = Attacher::AttachEngine3D
  Height = 18
  Placement = pos=(0,9,-8) rot=(1,0,0;1.5708rad)
  Radius = 4.2
FEATURE [Part::Box] Box001027006  label="Cube026"
  AttacherType = Attacher::AttachEngine3D
  Height = 17
  Length = 12
  Placement = pos=(-6,-7,-28) rot=(0,0,1;0rad)
  Width = 4.5
FEATURE [Part::Box] Box001027007  label="Cube027"
  AttacherType = Attacher::AttachEngine3D
  Height = 17
  Length = 12
  Placement = pos=(-6,2.5,-28) rot=(0,0,1;0rad)
  Width = 4.5
FEATURE [Part::MultiFuse] Fusion082  label="cut-holder-6"
  Shapes = -> [Fusion069,Box001027006]
FEATURE [Part::MultiFuse] Fusion083  label="cut-holder-base-4"
  Shapes = -> [Cut020,Box001027007]
FEATURE [Part::Fillet] Fillet008
  Base = -> Fusion083
  Edges = 1 edges r=5: [Edge12]
FEATURE [Part::Fillet] Fillet009
  Base = -> Fusion082
  Edges = 1 edges r=5: [Edge12]
FEATURE [Part::Fillet] Fillet010
  Base = -> Fillet008
  Edges = 1 edges r=3: [Edge36]
FEATURE [Part::Fillet] Fillet011
  Base = -> Fillet009
  Edges = 1 edges r=3: [Edge78]
FEATURE [Part::Cylinder] Cylinder068  label="rocker-007"
  Angle = 360
  AttacherType = Attacher::AttachEngine3D
  Height = 18
  Placement = pos=(0,9,-8) rot=(1,0,0;1.5708rad)
  Radius = 4.2
FEATURE [Part::Cut] Cut037  label="cut-holder-base-a"
  Base = -> Fillet010
  Tool = -> Cylinder067
FEATURE [Part::Cut] Cut038  label="cut-holder-a"
  Base = -> Fillet011
  Tool = -> Cylinder068
FEATURE [Part::Cylinder] Cylinder069  label="1251-spring"
  Angle = 360
  AttacherType = Attacher::AttachEngine3D
  Height = 10.6
  Placement = pos=(0,0,-44) rot=(0,0,1;0rad)
  Radius = 3.35
FEATURE [Part::Box] Box001027008  label="Cube028"
  AttacherType = Attacher::AttachEngine3D
  Height = 10.6
  Length = 15
  Placement = pos=(-11,-13,-38) rot=(0,0,1;0rad)
  Width = 24
FEATURE [Part::Box] Box001027009  label="Cube029"
  AttacherType = Attacher::AttachEngine3D
  Height = 10.6
  Length = 15
  Placement = pos=(-11,-13,-38) rot=(0,0,1;0rad)
  Width = 24
FEATURE [Part::Box] Box001027010  label="Cube030"
  AttacherType = Attacher::AttachEngine3D
  Height = 10.6
  Length = 15
  Placement = pos=(-11,-13,-38) rot=(0,0,1;0rad)
  Width = 24
FEATURE [Part::Cut] Cut039  label="cut-lever-x"
  Base = -> Fusion076
  Tool = -> Box001027008
FEATURE [Part::Cut] Cut040  label="cut-holder-base-b"
  Base = -> Cut037
  Tool = -> Box001027009
FEATURE [Part::Cut] Cut041  label="cut-holderx"
  Base = -> Cut038
  Tool = -> Box001027010
FEATURE [Part::Cylinder] Cylinder070  label="Cylinder066"
  Angle = 360
  AttacherType = Attacher::AttachEngine3D
  Height = 10
  Placement = pos=(17,10,-24) rot=(1,0,0;1.5708rad)
  Radius = 1.7
FEATURE [Part::Cylinder] Cylinder071  label="Cylinder067"
  Angle = 360
  AttacherType = Attacher::AttachEngine3D
  Height = 10
  Placement = pos=(33,10,-24) rot=(1,0,0;1.5708rad)
  Radius = 1.7
FEATURE [Part::MultiFuse] Fusion084  label="mounting-holes"
  Shapes = -> [Cylinder070,Cylinder071]
FEATURE [Part::Cut] Cut042
  Base = -> Cut040
  Tool = -> Fusion084
FEATURE [Part::Chamfer] Chamfer004  label="cut-holder-basex"
  Base = -> Cut042
  Edges = 2 edges r=2: [Edge160,Edge174]
FEATURE [Part::Box] Box001027011  label="Cube031"
  AttacherType = Attacher::AttachEngine3D
  Height = 43
  Length = 40
  Placement = pos=(35,0.2,-59) rot=(0,0,1;0rad)
  Width = 4
FEATURE [Part::Cylinder] Cylinder074  label="cutter-fit-cylinder"
  Angle = 360
  AttacherType = Attacher::AttachEngine3D
  Height = 21
  Placement = pos=(45,5,-26) rot=(1,0,0;1.5708rad)
  Radius = 3.2
FEATURE [Part::Box] Box001027012  label="Cube032"
  AttacherType = Attacher::AttachEngine3D
  Height = 13
  Length = 2
  Placement = pos=(0,-5,0) rot=(0,0,1;0rad)
  Width = 10
FEATURE [Part::Box] Box001027013  label="Cube033"
  AttacherType = Attacher::AttachEngine3D
  Height = 2
  Length = 13
  Placement = pos=(0,-5,0) rot=(0,-1,0;1.39626rad)
  Width = 10
FEATURE [Part::Cylinder] Cylinder075
  Angle = 360
  AttacherType = Attacher::AttachEngine3D
  Height = 13
  Placement = pos=(0,7,0) rot=(1,0,0;1.5708rad)
  Radius = 2
FEATURE [Part::Cylinder] Cylinder076
  Angle = 360
  AttacherType = Attacher::AttachEngine3D
  Height = 8
  Placement = pos=(0,4,0) rot=(1,0,0;1.5708rad)
  Radius = 8
FEATURE [Part::Cut] Cut043
  Base = -> Cylinder076
  Tool = -> Cylinder075
FEATURE [Part::MultiCommon] Common017
  Shapes = -> [Box001027012,Box001027013]
FEATURE [Part::MultiCommon] Common018
  Placement = pos=(50,0,11) rot=(0,-1,0;0.087266rad)
  Shapes = -> [Cut043,Common017]
FEATURE [Part::MultiCommon] Common019
  Placement = pos=(50.7765,0,10.8978) rot=(0,1,0;0.174533rad)
  Shapes = -> [Cut043,Common017]
FEATURE [Part::MultiCommon] Common020
  Placement = pos=(49.2235,0,10.8978) rot=(0,-1,0;0.349066rad)
  Shapes = -> [Cut043,Common017]
FEATURE [Part::MultiCommon] Common021
  Placement = pos=(51.5,0,10.5981) rot=(0,1,0;0.436332rad)
  Shapes = -> [Cut043,Common017]
FEATURE [Part::MultiCommon] Common022
  Placement = pos=(48.5,0,10.5981) rot=(0,-1,0;0.610865rad)
  Shapes = -> [Cut043,Common017]
FEATURE [Part::MultiFuse] Fusion085  label="strength-slots004"
  Placement = pos=(14,0,-38) rot=(0,0,1;0rad)
  Shapes = -> [Common018,Common021,Common020,Common019,Common022]
FEATURE [Part::Cylinder] Cylinder077  label="bearing-fit-cylinder"
  Angle = 360
  AttacherType = Attacher::AttachEngine3D
  Height = 21
  Placement = pos=(64,5,-31) rot=(1,0,0;1.5708rad)
  Radius = 4.6
FEATURE [Part::Box] Box001027014  label="Cube034"
  AttacherType = Attacher::AttachEngine3D
  Height = 19
  Length = 16
  Placement = pos=(2,0.2,-53) rot=(0,0,1;0rad)
  Width = 4
FEATURE [Part::Cylinder] Cylinder078
  Angle = 360
  AttacherType = Attacher::AttachEngine3D
  Height = 20
  Placement = pos=(11,10,-43.5) rot=(1,0,0;1.5708rad)
  Radius = 1.7
FEATURE [Part::Cylinder] Cylinder079
  Angle = 360
  AttacherType = Attacher::AttachEngine3D
  Height = 20
  Placement = pos=(5,10,-41.5) rot=(1,0,0;1.5708rad)
  Radius = 1.7
FEATURE [Part::Box] Box001027016  label="Cube036"
  AttacherType = Attacher::AttachEngine3D
  Height = 16.6
  Length = 15
  Placement = pos=(-11,-13,-44) rot=(0,0,1;0rad)
  Width = 24
FEATURE [Part::Box] Box001027017  label="Cube037"
  AttacherType = Attacher::AttachEngine3D
  Height = 2
  Length = 13
  Placement = pos=(0,-10,0) rot=(0,-1,0;1.39626rad)
  Width = 20
FEATURE [Part::Box] Box001027018  label="Cube038"
  AttacherType = Attacher::AttachEngine3D
  Height = 13
  Length = 2
  Placement = pos=(0,-10,0) rot=(0,0,1;0rad)
  Width = 20
FEATURE [Part::Cylinder] Cylinder080
  Angle = 360
  AttacherType = Attacher::AttachEngine3D
  Height = 26
  Placement = pos=(0,12,0) rot=(1,0,0;1.5708rad)
  Radius = 2
FEATURE [Part::Cylinder] Cylinder081
  Angle = 360
  AttacherType = Attacher::AttachEngine3D
  Height = 18
  Placement = pos=(0,9,0) rot=(1,0,0;1.5708rad)
  Radius = 8
FEATURE [Part::Cut] Cut044
  Base = -> Cylinder081
  Tool = -> Cylinder080
FEATURE [Part::MultiCommon] Common023  label="strength-slot-010"
  Placement = pos=(0,0,2.5) rot=(0,-1,0;0.087266rad)
  Shapes = -> [Box001027017,Box001027018,Cut044]
FEATURE [Part::MultiCommon] Common024  label="strength-slot-011"
  Placement = pos=(0.647048,0,2.41481) rot=(0,1,0;0.174533rad)
  Shapes = -> [Box001027017,Box001027018,Cut044]
FEATURE [Part::MultiCommon] Common025  label="strength-slot-012"
  Placement = pos=(1.25,0,2.16506) rot=(0,1,0;0.436332rad)
  Shapes = -> [Box001027017,Box001027018,Cut044]
FEATURE [Part::MultiCommon] Common026  label="strength-slot-013"
  Placement = pos=(-0.647048,0,2.41481) rot=(0,-1,0;0.349066rad)
  Shapes = -> [Box001027017,Box001027018,Cut044]
FEATURE [Part::MultiCommon] Common027  label="strength-slot-014"
  Placement = pos=(-1.25,0,2.16506) rot=(0,-1,0;0.610865rad)
  Shapes = -> [Box001027017,Box001027018,Cut044]
FEATURE [Part::MultiFuse] Fusion086  label="strength-slots005"
  Placement = pos=(55,0,-26) rot=(0,1,0;3.61283rad)
  Shapes = -> [Common023,Common024,Common025,Common026,Common027]
FEATURE [Part::Box] Box001027019  label="Cube039"
  AttacherType = Attacher::AttachEngine3D
  Height = 2
  Length = 13
  Placement = pos=(0,-10,0) rot=(0,-1,0;1.39626rad)
  Width = 20
FEATURE [Part::Box] Box001027020  label="Cube040"
  AttacherType = Attacher::AttachEngine3D
  Height = 13
  Length = 2
  Placement = pos=(0,-10,0) rot=(0,0,1;0rad)
  Width = 20
FEATURE [Part::Cylinder] Cylinder082
  Angle = 360
  AttacherType = Attacher::AttachEngine3D
  Height = 26
  Placement = pos=(0,12,0) rot=(1,0,0;1.5708rad)
  Radius = 2
FEATURE [Part::Cylinder] Cylinder083
  Angle = 360
  AttacherType = Attacher::AttachEngine3D
  Height = 18
  Placement = pos=(0,9,0) rot=(1,0,0;1.5708rad)
  Radius = 8
FEATURE [Part::Cut] Cut045
  Base = -> Cylinder083
  Tool = -> Cylinder082
FEATURE [Part::MultiCommon] Common028  label="strength-slot-015"
  Placement = pos=(0,0,2.5) rot=(0,-1,0;0.087266rad)
  Shapes = -> [Box001027019,Box001027020,Cut045]
FEATURE [Part::MultiCommon] Common029  label="strength-slot-016"
  Placement = pos=(0.647048,0,2.41481) rot=(0,1,0;0.174533rad)
  Shapes = -> [Box001027019,Box001027020,Cut045]
FEATURE [Part::MultiCommon] Common030  label="strength-slot-017"
  Placement = pos=(1.25,0,2.16506) rot=(0,1,0;0.436332rad)
  Shapes = -> [Box001027019,Box001027020,Cut045]
FEATURE [Part::MultiCommon] Common031  label="strength-slot-018"
  Placement = pos=(-0.647048,0,2.41481) rot=(0,-1,0;0.349066rad)
  Shapes = -> [Box001027019,Box001027020,Cut045]
FEATURE [Part::MultiCommon] Common032  label="strength-slot-019"
  Placement = pos=(-1.25,0,2.16506) rot=(0,-1,0;0.610865rad)
  Shapes = -> [Box001027019,Box001027020,Cut045]
FEATURE [Part::MultiFuse] Fusion087  label="strength-slots006"
  Placement = pos=(64.6339,0,-29.6405) rot=(0,1,0;0.436332rad)
  Shapes = -> [Common028,Common029,Common030,Common031,Common032]
FEATURE [Part::MultiFuse] Fusion091  label="M3-clearance"
  Placement = pos=(0,0,-6) rot=(0,0,1;0rad)
  Shapes = -> [Cylinder078,Cylinder079]
FEATURE [Part::Cylinder] Cylinder084  label="Cylinder159"
  Angle = 360
  AttacherType = Attacher::AttachEngine3D
  Height = 10
  Placement = pos=(68,10,-26) rot=(1,0,0;1.5708rad)
  Radius = 1.7
FEATURE [Part::Cylinder] Cylinder085  label="Cylinder160"
  Angle = 360
  AttacherType = Attacher::AttachEngine3D
  Height = 10
  Placement = pos=(47,10,-26) rot=(1,0,0;1.5708rad)
  Radius = 1.7
FEATURE [Part::Box] Box001027021  label="Cube041"
  AttacherType = Attacher::AttachEngine3D
  Height = 10.6
  Length = 15
  Placement = pos=(-11,-13,-38) rot=(0,0,1;0rad)
  Width = 24
FEATURE [Part::Cylinder] Cylinder086  label="rocker-008"
  Angle = 360
  AttacherType = Attacher::AttachEngine3D
  Height = 18
  Placement = pos=(0,9,-8) rot=(1,0,0;1.5708rad)
  Radius = 4.2
FEATURE [Part::Box] Box001027022  label="Cube042"
  AttacherType = Attacher::AttachEngine3D
  Height = 17
  Length = 12
  Placement = pos=(-6,2.5,-28) rot=(0,0,1;0rad)
  Width = 4.5
FEATURE [Part::Cylinder] Cylinder087
  Angle = 360
  AttacherType = Attacher::AttachEngine3D
  Height = 20
  Placement = pos=(35,10,-36) rot=(1,0,0;1.5708rad)
  Radius = 1.4
FEATURE [Part::Cylinder] Cylinder088
  Angle = 360
  AttacherType = Attacher::AttachEngine3D
  Height = 20
  Placement = pos=(26,10,-35) rot=(1,0,0;1.5708rad)
  Radius = 1.4
FEATURE [Part::Cylinder] Cylinder089
  Angle = 360
  AttacherType = Attacher::AttachEngine3D
  Height = 30
  Placement = pos=(30.5,0,-55) rot=(0,0,1;0rad)
  Radius = 1.4
FEATURE [Part::Cylinder] Cylinder090
  Angle = 360
  AttacherType = Attacher::AttachEngine3D
  Height = 20
  Placement = pos=(55,10,-26) rot=(1,0,0;1.5708rad)
  Radius = 3.2
FEATURE [Part::Cylinder] Cylinder091
  Angle = 360
  AttacherType = Attacher::AttachEngine3D
  Height = 20
  Placement = pos=(64,10,-31) rot=(1,0,0;1.5708rad)
  Radius = 1.7
FEATURE [Part::Box] Box001027024  label="Cube044"
  AttacherType = Attacher::AttachEngine3D
  Height = 25
  Length = 80
  Placement = pos=(-6,2.5,-29) rot=(0,1,0;0.20944rad)
  Width = 4.5
FEATURE [Part::Box] Box001027025  label="Cube045"
  AttacherType = Attacher::AttachEngine3D
  Height = 10
  Length = 21
  Placement = pos=(20,-2.5,-42) rot=(0,0,1;0rad)
  Width = 9.5
FEATURE [Part::Box] Box001027026  label="Cube046"
  AttacherType = Attacher::AttachEngine3D
  Height = 2
  Length = 13
  Placement = pos=(0,-10,0) rot=(0,-1,0;1.39626rad)
  Width = 20
FEATURE [Part::Box] Box001027027  label="Cube047"
  AttacherType = Attacher::AttachEngine3D
  Height = 13
  Length = 2
  Placement = pos=(0,-10,0) rot=(0,0,1;0rad)
  Width = 20
FEATURE [Part::Cylinder] Cylinder092
  Angle = 360
  AttacherType = Attacher::AttachEngine3D
  Height = 26
  Placement = pos=(0,12,0) rot=(1,0,0;1.5708rad)
  Radius = 2
FEATURE [Part::Cylinder] Cylinder093
  Angle = 360
  AttacherType = Attacher::AttachEngine3D
  Height = 18
  Placement = pos=(0,9,0) rot=(1,0,0;1.5708rad)
  Radius = 8
FEATURE [Part::Cut] Cut048
  Base = -> Cylinder093
  Tool = -> Cylinder092
FEATURE [Part::MultiCommon] Common033  label="strength-slot-020"
  Placement = pos=(0,0,2.5) rot=(0,-1,0;0.087266rad)
  Shapes = -> [Box001027026,Box001027027,Cut048]
FEATURE [Part::MultiCommon] Common034  label="strength-slot-021"
  Placement = pos=(0.647048,0,2.41481) rot=(0,1,0;0.174533rad)
  Shapes = -> [Box001027026,Box001027027,Cut048]
FEATURE [Part::MultiCommon] Common035  label="strength-slot-022"
  Placement = pos=(1.25,0,2.16506) rot=(0,1,0;0.436332rad)
  Shapes = -> [Box001027026,Box001027027,Cut048]
FEATURE [Part::MultiCommon] Common036  label="strength-slot-023"
  Placement = pos=(-0.647048,0,2.41481) rot=(0,-1,0;0.349066rad)
  Shapes = -> [Box001027026,Box001027027,Cut048]
FEATURE [Part::MultiCommon] Common037  label="strength-slot-024"
  Placement = pos=(-1.25,0,2.16506) rot=(0,-1,0;0.610865rad)
  Shapes = -> [Box001027026,Box001027027,Cut048]
FEATURE [Part::MultiFuse] Fusion093  label="strength-slots008"
  Placement = pos=(55,0,-26) rot=(0,1,0;0.436332rad)
  Shapes = -> [Common033,Common034,Common035,Common036,Common037]
FEATURE [Part::Box] Box001027028  label="Cube048"
  AttacherType = Attacher::AttachEngine3D
  Height = 2
  Length = 13
  Placement = pos=(0,-10,0) rot=(0,-1,0;1.39626rad)
  Width = 20
FEATURE [Part::Box] Box001027029  label="Cube049"
  AttacherType = Attacher::AttachEngine3D
  Height = 13
  Length = 2
  Placement = pos=(0,-10,0) rot=(0,0,1;0rad)
  Width = 20
FEATURE [Part::Cylinder] Cylinder094  label="Cylinder161"
  Angle = 360
  AttacherType = Attacher::AttachEngine3D
  Height = 26
  Placement = pos=(0,12,0) rot=(1,0,0;1.5708rad)
  Radius = 2
FEATURE [Part::Cylinder] Cylinder095  label="Cylinder162"
  Angle = 360
  AttacherType = Attacher::AttachEngine3D
  Height = 18
  Placement = pos=(0,9,0) rot=(1,0,0;1.5708rad)
  Radius = 8
FEATURE [Part::Cut] Cut049
  Base = -> Cylinder095
  Tool = -> Cylinder094
FEATURE [Part::MultiCommon] Common038  label="strength-slot-025"
  Placement = pos=(0,0,2.5) rot=(0,-1,0;0.087266rad)
  Shapes = -> [Box001027028,Box001027029,Cut049]
FEATURE [Part::MultiCommon] Common039  label="strength-slot-026"
  Placement = pos=(0.647048,0,2.41481) rot=(0,1,0;0.174533rad)
  Shapes = -> [Box001027028,Box001027029,Cut049]
FEATURE [Part::MultiCommon] Common040  label="strength-slot-027"
  Placement = pos=(1.25,0,2.16506) rot=(0,1,0;0.436332rad)
  Shapes = -> [Box001027028,Box001027029,Cut049]
FEATURE [Part::MultiCommon] Common041  label="strength-slot-028"
  Placement = pos=(-0.647048,0,2.41481) rot=(0,-1,0;0.349066rad)
  Shapes = -> [Box001027028,Box001027029,Cut049]
FEATURE [Part::MultiCommon] Common042  label="strength-slot-029"
  Placement = pos=(-1.25,0,2.16506) rot=(0,-1,0;0.610865rad)
  Shapes = -> [Box001027028,Box001027029,Cut049]
FEATURE [Part::MultiFuse] Fusion094  label="strength-slots009"
  Placement = pos=(65,0,-30) rot=(0,1,0;3.57793rad)
  Shapes = -> [Common038,Common039,Common040,Common041,Common042]
FEATURE [Part::Cylinder] Cylinder096
  Angle = 360
  AttacherType = Attacher::AttachEngine3D
  Height = 4.5
  Placement = pos=(55,7,-26) rot=(1,0,0;1.5708rad)
  Radius = 13
FEATURE [Part::Chamfer] Chamfer006
  Base = -> Box001027024
  Edges = 1 edges r=13: [Edge2]
FEATURE [Part::Chamfer] Chamfer007
  Base = -> Box001027025
  Edges = 2 edges r=5: [Edge2,Edge6]
FEATURE [Part::Fillet] Fillet013
  Base = -> Chamfer007
  Edges = 2 edges r=3: [Edge10,Edge18]
FEATURE [Part::Box] Box001027030  label="Cube050"
  AttacherType = Attacher::AttachEngine3D
  Height = 12
  Length = 25
  Placement = pos=(18,-5,-42) rot=(0,0,1;0rad)
  Width = 9.5
FEATURE [Part::MultiFuse] Fusion095  label="cut-holder-base-1"
  Shapes = -> [Cylinder096,Chamfer006,Box001027022]
FEATURE [Part::MultiFuse] Fusion096  label="mounting-holes001"
  Shapes = -> [Cylinder084,Cylinder085]
FEATURE [Part::MultiFuse] Fusion097  label="guillotine-and-fulcrum-holes"
  Shapes = -> [Fusion093,Fusion094,Cylinder091,Cylinder090]
FEATURE [Part::MultiFuse] Fusion098  label="common-holes"
  Shapes = -> [Fusion097,Box001027021]
FEATURE [Part::Cut] Cut050  label="cut-holder-blank-1"
  Base = -> Fusion095
  Tool = -> Fusion098
FEATURE [Part::Cut] Cut051  label="cut-holder-blank-2"
  Base = -> Cut050
  Tool = -> Cylinder086
FEATURE [Part::Fillet] Fillet014
  Base = -> Cut051
  Edges = 1 edges r=8: [Edge80]
FEATURE [Part::Fillet] Fillet015
  Base = -> Fillet014
  Edges = 1 edges r=10: [Edge36]
FEATURE [Part::Fillet] Fillet016
  Base = -> Fillet015
  Edges = 1 edges r=3: [Edge36]
FEATURE [Part::Fillet] Fillet017
  Base = -> Fillet016
  Edges = 1 edges r=10: [Edge117]
FEATURE [Part::Fillet] Fillet018  label="cut-holder-blank-3"
  Base = -> Fillet017
  Edges = 1 edges r=3: [Edge32]
FEATURE [Part::Cylinder] Cylinder097  label="rocker-cut"
  Angle = 360
  AttacherType = Attacher::AttachEngine3D
  Height = 18
  Placement = pos=(0,9,-8) rot=(1,0,0;1.5708rad)
  Radius = 4.2
FEATURE [Part::Box] Box001027033  label="Cube053"
  AttacherType = Attacher::AttachEngine3D
  Height = 25
  Length = 40
  Placement = pos=(32,-4.5,-33) rot=(0,1,0;0.366519rad)
  Width = 4.5
FEATURE [Part::Box] Box001027034  label="Cube054"
  AttacherType = Attacher::AttachEngine3D
  Height = 2
  Length = 13
  Placement = pos=(0,-10,0) rot=(0,-1,0;1.39626rad)
  Width = 20
FEATURE [Part::Box] Box001027035  label="Cube055"
  AttacherType = Attacher::AttachEngine3D
  Height = 13
  Length = 2
  Placement = pos=(0,-10,0) rot=(0,0,1;0rad)
  Width = 20
FEATURE [Part::Cylinder] Cylinder100
  Angle = 360
  AttacherType = Attacher::AttachEngine3D
  Height = 26
  Placement = pos=(0,12,0) rot=(1,0,0;1.5708rad)
  Radius = 2
FEATURE [Part::Cylinder] Cylinder101
  Angle = 360
  AttacherType = Attacher::AttachEngine3D
  Height = 18
  Placement = pos=(0,9,0) rot=(1,0,0;1.5708rad)
  Radius = 8
FEATURE [Part::Cut] Cut052
  Base = -> Cylinder101
  Tool = -> Cylinder100
FEATURE [Part::MultiCommon] Common043  label="strength-slot-030"
  Placement = pos=(0,0,2.5) rot=(0,-1,0;0.087266rad)
  Shapes = -> [Box001027034,Box001027035,Cut052]
FEATURE [Part::MultiCommon] Common044  label="strength-slot-031"
  Placement = pos=(0.647048,0,2.41481) rot=(0,1,0;0.174533rad)
  Shapes = -> [Box001027034,Box001027035,Cut052]
FEATURE [Part::MultiCommon] Common045  label="strength-slot-032"
  Placement = pos=(1.25,0,2.16506) rot=(0,1,0;0.436332rad)
  Shapes = -> [Box001027034,Box001027035,Cut052]
FEATURE [Part::MultiCommon] Common046  label="strength-slot-033"
  Placement = pos=(-0.647048,0,2.41481) rot=(0,-1,0;0.349066rad)
  Shapes = -> [Box001027034,Box001027035,Cut052]
FEATURE [Part::MultiCommon] Common047  label="strength-slot-034"
  Placement = pos=(-1.25,0,2.16506) rot=(0,-1,0;0.610865rad)
  Shapes = -> [Box001027034,Box001027035,Cut052]
FEATURE [Part::MultiFuse] Fusion099  label="strength-slots010"
  Placement = pos=(55,0,-26) rot=(0,1,0;0.436332rad)
  Shapes = -> [Common043,Common044,Common045,Common046,Common047]
FEATURE [Part::Box] Box001027036  label="Cube056"
  AttacherType = Attacher::AttachEngine3D
  Height = 2
  Length = 13
  Placement = pos=(0,-10,0) rot=(0,-1,0;1.39626rad)
  Width = 20
FEATURE [Part::Box] Box001027037  label="Cube057"
  AttacherType = Attacher::AttachEngine3D
  Height = 13
  Length = 2
  Placement = pos=(0,-10,0) rot=(0,0,1;0rad)
  Width = 20
FEATURE [Part::Cylinder] Cylinder102  label="Cylinder165"
  Angle = 360
  AttacherType = Attacher::AttachEngine3D
  Height = 26
  Placement = pos=(0,12,0) rot=(1,0,0;1.5708rad)
  Radius = 2
FEATURE [Part::Cylinder] Cylinder103  label="Cylinder166"
  Angle = 360
  AttacherType = Attacher::AttachEngine3D
  Height = 18
  Placement = pos=(0,9,0) rot=(1,0,0;1.5708rad)
  Radius = 8
FEATURE [Part::Cut] Cut053
  Base = -> Cylinder103
  Tool = -> Cylinder102
FEATURE [Part::MultiCommon] Common048  label="strength-slot-035"
  Placement = pos=(0,0,2.5) rot=(0,-1,0;0.087266rad)
  Shapes = -> [Box001027036,Box001027037,Cut053]
FEATURE [Part::MultiCommon] Common049  label="strength-slot-036"
  Placement = pos=(0.647048,0,2.41481) rot=(0,1,0;0.174533rad)
  Shapes = -> [Box001027036,Box001027037,Cut053]
FEATURE [Part::MultiCommon] Common050  label="strength-slot-037"
  Placement = pos=(1.25,0,2.16506) rot=(0,1,0;0.436332rad)
  Shapes = -> [Box001027036,Box001027037,Cut053]
FEATURE [Part::MultiCommon] Common051  label="strength-slot-038"
  Placement = pos=(-0.647048,0,2.41481) rot=(0,-1,0;0.349066rad)
  Shapes = -> [Box001027036,Box001027037,Cut053]
FEATURE [Part::MultiCommon] Common052  label="strength-slot-039"
  Placement = pos=(-1.25,0,2.16506) rot=(0,-1,0;0.610865rad)
  Shapes = -> [Box001027036,Box001027037,Cut053]
FEATURE [Part::MultiFuse] Fusion100  label="strength-slots011"
  Placement = pos=(65,0,-30) rot=(0,1,0;3.57793rad)
  Shapes = -> [Common048,Common049,Common050,Common051,Common052]
FEATURE [Part::Cut] Cut056  label="cut-holder-base-006"
  Base = -> Fillet018
  Tool = -> Fusion096
FEATURE [Part::Chamfer] Chamfer009  label="cut-holder-base-7"
  Base = -> Cut056
  Edges = 4 edges r=2.5: [Edge13,Edge14,Edge88,Edge109]
FEATURE [Part::MultiFuse] Fusion104  label="cut-holder-base-007"
  Shapes = -> [Chamfer009,Fillet013]
FEATURE [Part::MultiFuse] Fusion105  label="base-block-holes"
  Shapes = -> [Cylinder087,Cylinder088,Cylinder089]
FEATURE [Part::Cut] Cut057  label="cut-holder-base"
  Base = -> Fusion104
  Tool = -> Fusion105
FEATURE [Part::Cylinder] Cylinder105
  Angle = 360
  AttacherType = Attacher::AttachEngine3D
  Height = 20
  Placement = pos=(26,10,-35) rot=(1,0,0;1.5708rad)
  Radius = 1.7
FEATURE [Part::Cylinder] Cylinder106
  Angle = 360
  AttacherType = Attacher::AttachEngine3D
  Height = 20
  Placement = pos=(35,10,-36) rot=(1,0,0;1.5708rad)
  Radius = 1.7
FEATURE [Part::MultiFuse] Fusion107  label="adjuster-M3-holes"
  Shapes = -> [Cylinder106,Cylinder105]
FEATURE [Part::Chamfer] Chamfer010
  Base = -> Box001027030
  Edges = 2 edges r=5: [Edge2,Edge6]
FEATURE [Part::Fillet] Fillet025  label="Adjuster-hole"
  Base = -> Chamfer010
  Edges = 4 edges r=3: [Edge2,Edge10,Edge17,Edge18]
  Placement = pos=(-11,0,7) rot=(0,0,1;0rad)
FEATURE [Part::Chamfer] Chamfer011  label="bearing-clamp"
  Base = -> Cut036
  Edges = 1 edges r=2: [Edge43]
FEATURE [Part::Chamfer] Chamfer014  label="gearbox"
  Base = -> Cut007
  Edges = 5 edges r=0.5: [Edge16,Edge17,Edge18,Edge19,Edge20]
FEATURE [Part::Feature] Box001027038
  Placement = pos=(5.83013,0.0980762,-77) rot=(0,0,1;1.0472rad)
  shape: bbox 13.66 x 13.66 x 25 mm, 6 faces (baked)
FEATURE [Part::Feature] Box001027039
  Placement = pos=(2.83013,5.09808,-77) rot=(0,0,1;2.0944rad)
  shape: bbox 13.66 x 13.66 x 25 mm, 6 faces (baked)
FEATURE [Part::Feature] Box001027040
  Placement = pos=(-3,5,-77) rot=(0,0,1;3.14159rad)
  shape: bbox 10 x 10 x 25 mm, 6 faces (baked)
FEATURE [Part::Feature] Box001027041
  Placement = pos=(-5.83013,-0.0980762,-77) rot=(0,0,1;4.18879rad)
  shape: bbox 13.66 x 13.66 x 25 mm, 6 faces (baked)
FEATURE [Part::Feature] Box001027042
  Placement = pos=(-2.83013,-5.09808,-77) rot=(0,0,-1;1.0472rad)
  shape: bbox 13.66 x 13.66 x 25 mm, 6 faces (baked)
FEATURE [Part::MultiFuse] Fusion110
  Shapes = -> [Box001027,Box001027038,Box001027041,Box001027040,Box001027039,Box001027042]
FEATURE [Part::Cut] Cut062  label="m3-nut-1"
  Base = -> Cylinder064
  Tool = -> Fusion110
FEATURE [Part::Cut] Cut063  label="rocker"
  Base = -> Cut032
  Placement = pos=(0,0,-6) rot=(0,0,1;0rad)
  Tool = -> Cut062
FEATURE [Part::Feature] Part__Feature068  label="M6 thread001"
  Placement = pos=(55,-7,-26) rot=(1,0,0;1.5708rad)
  shape: bbox 11.55 x 5.798 x 10 mm, 23 faces (baked)
FEATURE [Part::Cylinder] Cylinder108  label="Cylinder168"
  Angle = 360
  AttacherType = Attacher::AttachEngine3D
  Height = 8
  Placement = pos=(0,0,-11) rot=(0,0,1;0rad)
  Radius = 2.2
FEATURE [Part::Torus] Torus
  Angle1 = -180
  Angle2 = 180
  Angle3 = 360
  AttacherType = Attacher::AttachEngine3D
  Placement = pos=(0,20,0) rot=(0,1,0;1.5708rad)
  Radius1 = 20
  Radius2 = 1.1
FEATURE [Part::Feature] Part__Feature069  label="M6 thread002"
  Placement = pos=(0,7.89305,16.686) rot=(-1,0,0;0.698132rad)
  shape: bbox 11.55 x 10.62 x 10 mm, 23 faces (baked)
FEATURE [Part::Cylinder] Cylinder109  label="Cylinder169"
  Angle = 360
  AttacherType = Attacher::AttachEngine3D
  Height = 10
  Placement = pos=(0,4.67911,12.8558) rot=(-1,0,0;0.698132rad)
  Radius = 2.2
FEATURE [Part::Torus] Torus001
  Angle1 = -180
  Angle2 = 180
  Angle3 = 360
  AttacherType = Attacher::AttachEngine3D
  Placement = pos=(0,20,0) rot=(0,1,0;1.5708rad)
  Radius1 = 20
  Radius2 = 2.2
FEATURE [Part::Feature] Part__Feature070  label="tree-output-thread"
  Placement = pos=(0,0,-10) rot=(0,0,1;0rad)
  shape: bbox 11.55 x 10 x 5.798 mm, 23 faces (baked)
FEATURE [Part::Cone] Cone
  Angle = 360
  AttacherType = Attacher::AttachEngine3D
  Height = 2
  Placement = pos=(0,3.71769,11.6141) rot=(-1,0,0;0.619592rad)
  Radius1 = 1.1
  Radius2 = 1.3
FEATURE [Part::Box] Box001027043  label="Cube058"
  AttacherType = Attacher::AttachEngine3D
  Height = 22
  Length = 10
  Placement = pos=(-5,-4,0) rot=(0,0,1;0rad)
  Width = 24
FEATURE [Part::Box] Box001027044  label="Cube059"
  AttacherType = Attacher::AttachEngine3D
  Height = 22
  Length = 10
  Placement = pos=(-5,0.461228,13.9369) rot=(-1,0,0;0.619592rad)
  Width = 24
FEATURE [Part::MultiCommon] Common053
  Shapes = -> [Torus,Box001027043]
FEATURE [Part::Cut] Cut064
  Base = -> Common053
  Tool = -> Box001027044
FEATURE [Part::Cylinder] Cylinder111  label="Cylinder170"
  Angle = 360
  AttacherType = Attacher::AttachEngine3D
  Height = 6
  Placement = pos=(0,7.57166,16.303) rot=(-1,0,0;0.698132rad)
  Radius = 4
FEATURE [Part::Cylinder] Cylinder112  label="base-thread-hole"
  Angle = 360
  AttacherType = Attacher::AttachEngine3D
  Height = 6
  Placement = pos=(0,0,-10.5) rot=(0,0,1;0rad)
  Radius = 4
FEATURE [Part::MultiFuse] Fusion112  label="torroidal-hole"
  Shapes = -> [Cylinder109,Cone,Cut064,Cylinder111]
FEATURE [Part::Feature] Fusion112001
  Placement = pos=(0,0,0) rot=(0,0,1;1.0472rad)
  shape: bbox 15.77 x 11.42 x 23.47 mm, 8 faces (baked)
FEATURE [Part::Feature] Fusion112002
  Placement = pos=(0,0,0) rot=(0,0,1;2.0944rad)
  shape: bbox 15.77 x 11.42 x 23.47 mm, 8 faces (baked)
FEATURE [Part::Feature] Fusion112003
  Placement = pos=(0,0,0) rot=(0,0,1;3.14159rad)
  shape: bbox 8 x 17.33 x 23.47 mm, 8 faces (baked)
FEATURE [Part::Feature] Fusion112004
  Placement = pos=(0,0,0) rot=(0,0,1;4.18879rad)
  shape: bbox 15.77 x 11.42 x 23.47 mm, 8 faces (baked)
FEATURE [Part::Feature] Fusion112005
  Placement = pos=(0,0,0) rot=(0,0,-1;1.0472rad)
  shape: bbox 15.77 x 11.42 x 23.47 mm, 8 faces (baked)
FEATURE [Part::MultiFuse] Fusion112006
  Shapes = -> [Fusion112,Fusion112002,Fusion112003,Fusion112001,Fusion112005,Fusion112004]
FEATURE [Part::Feature] Part__Feature069001
  Placement = pos=(-6.83558,3.94652,16.686) rot=(-0.509677,-0.294262,0.808479;1.24028rad)
  shape: bbox 12.08 x 11.48 x 10 mm, 23 faces (baked)
FEATURE [Part::Feature] Part__Feature069002
  Placement = pos=(-6.83558,-3.94652,16.686) rot=(-0.193725,-0.335541,0.921891;2.16336rad)
  shape: bbox 12.08 x 11.48 x 10 mm, 23 faces (baked)
FEATURE [Part::Feature] Part__Feature069003
  Placement = pos=(0,-7.89305,16.686) rot=(0,-0.34202,0.939693;3.14159rad)
  shape: bbox 11.55 x 10.62 x 10 mm, 23 faces (baked)
FEATURE [Part::Feature] Part__Feature069004
  Placement = pos=(6.83558,-3.94652,16.686) rot=(0.193725,-0.335541,0.921891;4.11983rad)
  shape: bbox 12.08 x 11.48 x 10 mm, 23 faces (baked)
FEATURE [Part::Feature] Part__Feature069005
  Placement = pos=(6.83558,3.94652,16.686) rot=(-0.509677,0.294262,-0.808479;1.24028rad)
  shape: bbox 12.08 x 11.48 x 10 mm, 23 faces (baked)
FEATURE [Part::MultiFuse] Fusion112008  label="6-M6-threads-top"
  Shapes = -> [Part__Feature069001,Part__Feature069003,Part__Feature069002,Part__Feature069004,Part__Feature069005,Part__Feature069]
FEATURE [Part::Sphere] Sphere
  Angle1 = -90
  Angle2 = 90
  Angle3 = 360
  AttacherType = Attacher::AttachEngine3D
  Radius = 22
FEATURE [Part::Box] Box001027045  label="Cube060"
  AttacherType = Attacher::AttachEngine3D
  Height = 60
  Length = 30
  Placement = pos=(15,-20,-16) rot=(0,0,1;0rad)
  Width = 40
FEATURE [Part::Feature] Box001027045001
  Placement = pos=(24.7487,-3.53553,-16) rot=(0,0,1;0.785398rad)
  shape: bbox 49.5 x 49.5 x 60 mm, 6 faces (baked)
FEATURE [Part::Feature] Box001027045002
  Placement = pos=(20,15,-16) rot=(0,0,1;1.5708rad)
  shape: bbox 40 x 30 x 60 mm, 6 faces (baked)
FEATURE [Part::Feature] Box001027045003
  Placement = pos=(3.53553,24.7487,-16) rot=(0,0,1;2.35619rad)
  shape: bbox 49.5 x 49.5 x 60 mm, 6 faces (baked)
FEATURE [Part::Feature] Box001027045004
  Placement = pos=(-15,20,-16) rot=(0,0,1;3.14159rad)
  shape: bbox 30 x 40 x 60 mm, 6 faces (baked)
FEATURE [Part::Feature] Box001027045005
  Placement = pos=(-24.7487,3.53553,-16) rot=(0,0,1;3.92699rad)
  shape: bbox 49.5 x 49.5 x 60 mm, 6 faces (baked)
FEATURE [Part::Feature] Box001027045006
  Placement = pos=(-20,-15,-16) rot=(0,0,-1;1.5708rad)
  shape: bbox 40 x 30 x 60 mm, 6 faces (baked)
FEATURE [Part::Feature] Box001027045007
  Placement = pos=(-3.53553,-24.7487,-16) rot=(0,0,-1;0.785398rad)
  shape: bbox 49.5 x 49.5 x 60 mm, 6 faces (baked)
FEATURE [Part::MultiFuse] Fusion112010  label="octagonal-cut"
  Shapes = -> [Box001027045007,Box001027045006,Box001027045001,Box001027045004,Box001027045,Box001027045002,Box001027045003,Box001027045005]
FEATURE [Part::Box] Box001027045008  label="Cube061"
  AttacherType = Attacher::AttachEngine3D
  Height = 50
  Length = 60
  Placement = pos=(-30,-30,-60) rot=(0,0,1;0rad)
  Width = 60
FEATURE [Part::Cylinder] Cylinder113  label="Cylinder171"
  Angle = 360
  AttacherType = Attacher::AttachEngine3D
  Height = 10
  Placement = pos=(0,0,-2) rot=(0,0,1;0rad)
  Radius = 0.7
FEATURE [Part::Cylinder] Cylinder114  label="Cylinder172"
  Angle = 360
  AttacherType = Attacher::AttachEngine3D
  Height = 26
  Placement = pos=(-8,0,-18) rot=(0,0,1;0rad)
  Radius = 1.7
FEATURE [Part::Cylinder] Cylinder115  label="Cylinder173"
  Angle = 360
  AttacherType = Attacher::AttachEngine3D
  Height = 26
  Placement = pos=(13,0,-18) rot=(0,0,1;0rad)
  Radius = 1.7
FEATURE [Part::Cylinder] Cylinder116  label="Cylinder174"
  Angle = 360
  AttacherType = Attacher::AttachEngine3D
  Height = 15
  Placement = pos=(9,5,-18) rot=(0,0,1;0rad)
  Radius = 3.8
FEATURE [Part::Cone] Cone001
  Angle = 360
  AttacherType = Attacher::AttachEngine3D
  Height = 3.8
  Placement = pos=(9,5,-3) rot=(0,0,1;0rad)
  Radius1 = 3.8
  Radius2 = 0
FEATURE [Part::MultiFuse] Fusion112012  label="fulcrum-hole"
  Placement = pos=(0,0,-3) rot=(0,0,1;0rad)
  Shapes = -> [Cylinder116,Cone001]
FEATURE [Part::Cylinder] Cylinder117  label="Cylinder175"
  Angle = 360
  AttacherType = Attacher::AttachEngine3D
  Height = 21
  Placement = pos=(13,0,-10) rot=(0,0,1;0rad)
  Radius = 5
FEATURE [Part::Box] Box001027045009  label="Cube062"
  AttacherType = Attacher::AttachEngine3D
  Height = 2.7
  Length = 10
  Placement = pos=(9.5,-2.9,0) rot=(0,0,1;0rad)
  Width = 5.8
FEATURE [Part::Box] Box001027045010  label="Cube063"
  AttacherType = Attacher::AttachEngine3D
  Height = 2.7
  Length = 13.5
  Placement = pos=(-18,-2.9,0) rot=(0,0,1;0rad)
  Width = 5.8
FEATURE [Part::MultiFuse] Fusion112014  label="m3-nut-hole-1"
  Shapes = -> [Cylinder114,Box001027045010]
FEATURE [Part::MultiFuse] Fusion112015  label="m3-nut-hole-2"
  Shapes = -> [Box001027045009,Cylinder115]
FEATURE [Part::MultiFuse] Fusion112016  label="m3-nut-holes"
  Shapes = -> [Fusion112014,Fusion112015]
FEATURE [Part::Cylinder] Cylinder118  label="Cylinder176"
  Angle = 360
  AttacherType = Attacher::AttachEngine3D
  Height = 8
  Placement = pos=(0,0,-7) rot=(0,0,1;0rad)
  Radius = 1.1
FEATURE [Part::MultiFuse] Fusion112017  label="torroidal-chanels-with-base-1"
  Shapes = -> [Fusion112006,Cylinder108,Cylinder118]
FEATURE [Part::Cut] Cut065
  Base = -> Sphere
  Tool = -> Box001027045008
FEATURE [Part::Cut] Cut066
  Base = -> Cut065
  Tool = -> Fusion112010
FEATURE [Part::MultiFuse] Fusion112018  label="merge-blank-2"
  Shapes = -> [Cylinder117,Cut066]
FEATURE [Part::MultiFuse] Fusion112019  label="base-holes"
  Shapes = -> [Fusion112012,Fusion112016]
FEATURE [Part::MultiFuse] Fusion112020  label="torroidal-channels-with-base-2"
  Shapes = -> [Fusion112017,Cylinder113]
FEATURE [Part::MultiFuse] Fusion112021  label="all-cavities"
  Shapes = -> [Fusion112020,Fusion112019]
FEATURE [Part::Cut] Cut067  label="merge-1"
  Base = -> Fusion112018
  Tool = -> Fusion112021
FEATURE [Part::MultiFuse] Fusion112022  label="mergerx"
  Shapes = -> [Cut067,Fusion112008]
FEATURE [Part::Cylinder] Cylinder119  label="Cylinder177"
  Angle = 360
  AttacherType = Attacher::AttachEngine3D
  Height = 9
  Placement = pos=(0,0,-12) rot=(0,0,1;0rad)
  Radius = 2.2
FEATURE [Part::Torus] Torus002
  Angle1 = -180
  Angle2 = 180
  Angle3 = 360
  AttacherType = Attacher::AttachEngine3D
  Placement = pos=(0,20,0) rot=(0,1,0;1.5708rad)
  Radius1 = 20
  Radius2 = 1.1
FEATURE [Part::Feature] Part__Feature069006  label="M6 thread003"
  Placement = pos=(0,7.89305,16.686) rot=(-1,0,0;0.698132rad)
  shape: bbox 11.55 x 10.62 x 10 mm, 23 faces (baked)
FEATURE [Part::Cylinder] Cylinder120  label="Cylinder178"
  Angle = 360
  AttacherType = Attacher::AttachEngine3D
  Height = 10
  Placement = pos=(0,4.67911,12.8558) rot=(-1,0,0;0.698132rad)
  Radius = 2.2
FEATURE [Part::Cone] Cone002
  Angle = 360
  AttacherType = Attacher::AttachEngine3D
  Height = 2
  Placement = pos=(0,3.71769,11.6141) rot=(-1,0,0;0.619592rad)
  Radius1 = 1.1
  Radius2 = 1.3
FEATURE [Part::Box] Box001027045011  label="Cube064"
  AttacherType = Attacher::AttachEngine3D
  Height = 22
  Length = 10
  Placement = pos=(-5,-4,0) rot=(0,0,1;0rad)
  Width = 24
FEATURE [Part::Box] Box001027045012  label="Cube065"
  AttacherType = Attacher::AttachEngine3D
  Height = 22
  Length = 10
  Placement = pos=(-5,0.461228,13.9369) rot=(-1,0,0;0.619592rad)
  Width = 24
FEATURE [Part::MultiCommon] Common054
  Shapes = -> [Torus002,Box001027045011]
FEATURE [Part::Cut] Cut068
  Base = -> Common054
  Tool = -> Box001027045012
FEATURE [Part::Cylinder] Cylinder121  label="Cylinder179"
  Angle = 360
  AttacherType = Attacher::AttachEngine3D
  Height = 6
  Placement = pos=(0,7.57166,16.303) rot=(-1,0,0;0.698132rad)
  Radius = 4
FEATURE [Part::Cylinder] Cylinder122  label="Cylinder180"
  Angle = 360
  AttacherType = Attacher::AttachEngine3D
  Height = 61
  Placement = pos=(0,0,-6) rot=(0,0,1;0rad)
  Radius = 1.1
FEATURE [Part::Torus] Torus003
  Angle1 = -180
  Angle2 = 180
  Angle3 = 360
  AttacherType = Attacher::AttachEngine3D
  Placement = pos=(0,20,0) rot=(0,1,0;1.5708rad)
  Radius1 = 20
  Radius2 = 1.1
FEATURE [Part::Feature] Part__Feature069007  label="M6 thread004"
  Placement = pos=(0,-7.89305,27.686) rot=(0,-0.34202,0.939693;3.14159rad)
  shape: bbox 11.55 x 10.62 x 10 mm, 23 faces (baked)
FEATURE [Part::Cylinder] Cylinder123  label="Cylinder181"
  Angle = 360
  AttacherType = Attacher::AttachEngine3D
  Height = 10
  Placement = pos=(0,4.67911,12.8558) rot=(-1,0,0;0.698132rad)
  Radius = 2.2
FEATURE [Part::Cone] Cone003
  Angle = 360
  AttacherType = Attacher::AttachEngine3D
  Height = 2
  Placement = pos=(0,3.71769,11.6141) rot=(-1,0,0;0.619592rad)
  Radius1 = 1.1
  Radius2 = 1.3
FEATURE [Part::Box] Box001027045013  label="Cube066"
  AttacherType = Attacher::AttachEngine3D
  Height = 22
  Length = 10
  Placement = pos=(-5,-4,0) rot=(0,0,1;0rad)
  Width = 24
FEATURE [Part::Box] Box001027045014  label="Cube067"
  AttacherType = Attacher::AttachEngine3D
  Height = 22
  Length = 10
  Placement = pos=(-5,0.461228,13.9369) rot=(-1,0,0;0.619592rad)
  Width = 24
FEATURE [Part::MultiCommon] Common055
  Shapes = -> [Torus003,Box001027045013]
FEATURE [Part::Cut] Cut069
  Base = -> Common055
  Tool = -> Box001027045014
FEATURE [Part::Cylinder] Cylinder124  label="Cylinder182"
  Angle = 360
  AttacherType = Attacher::AttachEngine3D
  Height = 6
  Placement = pos=(0,7.57166,16.303) rot=(-1,0,0;0.698132rad)
  Radius = 4
FEATURE [Part::Feature] Part__Feature069008  label="M6 thread005"
  Placement = pos=(0,7.89305,38.686) rot=(-1,0,0;0.698132rad)
  shape: bbox 11.55 x 10.62 x 10 mm, 23 faces (baked)
FEATURE [Part::Feature] Part__Feature069009  label="M6 thread006"
  Placement = pos=(0,-7.89305,49.686) rot=(0,-0.34202,0.939693;3.14159rad)
  shape: bbox 11.55 x 10.62 x 10 mm, 23 faces (baked)
FEATURE [Part::Feature] Part__Feature069010  label="M6 thread007"
  Placement = pos=(0,7.89305,60.686) rot=(-1,0,0;0.698132rad)
  shape: bbox 11.55 x 10.62 x 10 mm, 23 faces (baked)
FEATURE [Part::MultiFuse] Fusion112027  label="torroidal-hole005"
  Placement = pos=(0,0,44) rot=(0,0,1;0rad)
  Shapes = -> [Cylinder120,Cone002,Cut068,Cylinder121]
FEATURE [Part::Feature] Part__Feature069011  label="M6 thread008"
  Placement = pos=(0,-7.89305,71.686) rot=(0,-0.34202,0.939693;3.14159rad)
  shape: bbox 11.55 x 10.62 x 10 mm, 23 faces (baked)
FEATURE [Part::MultiFuse] Fusion112028  label="torroidal-hole006"
  Placement = pos=(0,0,55) rot=(0,0,1;3.14159rad)
  Shapes = -> [Cylinder123,Cone003,Cut069,Cylinder124]
FEATURE [Part::Cylinder] Cylinder125  label="Cylinder183"
  Angle = 360
  AttacherType = Attacher::AttachEngine3D
  Height = 26
  Placement = pos=(-8,0,-18) rot=(0,0,1;0rad)
  Radius = 1.7
FEATURE [Part::Cylinder] Cylinder126  label="Cylinder184"
  Angle = 360
  AttacherType = Attacher::AttachEngine3D
  Height = 26
  Placement = pos=(13,0,-18) rot=(0,0,1;0rad)
  Radius = 1.7
FEATURE [Part::Cylinder] Cylinder127  label="Cylinder185"
  Angle = 360
  AttacherType = Attacher::AttachEngine3D
  Height = 15
  Placement = pos=(9,5,-18) rot=(0,0,1;0rad)
  Radius = 3.8
FEATURE [Part::Cone] Cone004
  Angle = 360
  AttacherType = Attacher::AttachEngine3D
  Height = 3.8
  Placement = pos=(9,5,-3) rot=(0,0,1;0rad)
  Radius1 = 3.8
  Radius2 = 0
FEATURE [Part::MultiFuse] Fusion112029  label="fulcrum-hole001"
  Placement = pos=(0,0,-3) rot=(0,0,1;0rad)
  Shapes = -> [Cylinder127,Cone004]
FEATURE [Part::Box] Box001027045015  label="Cube068"
  AttacherType = Attacher::AttachEngine3D
  Height = 2.7
  Length = 10
  Placement = pos=(9.5,-2.9,0) rot=(0,0,1;0rad)
  Width = 5.8
FEATURE [Part::Box] Box001027045016  label="Cube069"
  AttacherType = Attacher::AttachEngine3D
  Height = 2.7
  Length = 13.5
  Placement = pos=(-18,-2.9,0) rot=(0,0,1;0rad)
  Width = 5.8
FEATURE [Part::MultiFuse] Fusion112030  label="m3-nut-hole-003"
  Shapes = -> [Cylinder125,Box001027045016]
FEATURE [Part::MultiFuse] Fusion112031  label="m3-nut-hole-004"
  Shapes = -> [Box001027045015,Cylinder126]
FEATURE [Part::MultiFuse] Fusion112032  label="m3-nut-holes001"
  Shapes = -> [Fusion112030,Fusion112031]
FEATURE [Part::MultiFuse] Fusion112033  label="base-holes001"
  Placement = pos=(0,0,0) rot=(0,0,1;1.5708rad)
  Shapes = -> [Fusion112029,Fusion112032]
FEATURE [Part::Box] Box001027045017  label="Cube070"
  AttacherType = Attacher::AttachEngine3D
  Height = 90
  Length = 16
  Placement = pos=(-8,-16,-11) rot=(0,0,1;0rad)
  Width = 32
FEATURE [Part::Box] Box001027045018  label="Cube071"
  AttacherType = Attacher::AttachEngine3D
  Height = 30
  Length = 21
  Placement = pos=(-11,-16.5,27.4) rot=(1,0,0;0.698132rad)
  Width = 13
FEATURE [Part::Box] Box001027045019  label="Cube072"
  AttacherType = Attacher::AttachEngine3D
  Height = 30
  Length = 21
  Placement = pos=(11,16.5,38.4) rot=(0,0.34202,0.939693;3.14159rad)
  Width = 13
FEATURE [Part::Box] Box001027045020  label="Cube073"
  AttacherType = Attacher::AttachEngine3D
  Height = 30
  Length = 21
  Placement = pos=(11,16.5,60.4) rot=(0,0.34202,0.939693;3.14159rad)
  Width = 39
FEATURE [Part::Box] Box001027045021  label="Cube074"
  AttacherType = Attacher::AttachEngine3D
  Height = 30
  Length = 21
  Placement = pos=(11,16.5,16.4) rot=(0,0.34202,0.939693;3.14159rad)
  Width = 13
FEATURE [Part::Box] Box001027045022  label="Cube075"
  AttacherType = Attacher::AttachEngine3D
  Height = 30
  Length = 21
  Placement = pos=(-11,-16.5,49.4) rot=(1,0,0;0.698132rad)
  Width = 13
FEATURE [Part::Box] Box001027045024  label="Cube077"
  AttacherType = Attacher::AttachEngine3D
  Height = 30
  Length = 21
  Placement = pos=(-11,-16.5,71.4) rot=(1,0,0;0.698132rad)
  Width = 13
FEATURE [Part::MultiFuse] Fusion112034
  Shapes = -> [Box001027045020,Box001027045018,Box001027045019,Box001027045021,Box001027045022,Box001027045024]
FEATURE [Part::Cut] Cut070
  Base = -> Box001027045017
  Tool = -> Fusion112034
FEATURE [Part::Cylinder] Cylinder128  label="Cylinder186"
  Angle = 360
  AttacherType = Attacher::AttachEngine3D
  Height = 10
  Placement = pos=(-5,9,-11) rot=(0,0,1;0rad)
  Radius = 6
FEATURE [Part::MultiFuse] Fusion112035
  Shapes = -> [Cut070,Cylinder128]
FEATURE [Part::Cylinder] Cylinder129  label="Cylinder187"
  Angle = 360
  AttacherType = Attacher::AttachEngine3D
  Height = 21
  Placement = pos=(0,13,-11) rot=(0,0,1;0rad)
  Radius = 5
FEATURE [Part::MultiFuse] Fusion112036  label="body-blank"
  Shapes = -> [Cylinder129,Fusion112035]
FEATURE [Part::MultiFuse] Fusion112043  label="M6-threads"
  Shapes = -> [Part__Feature069006,Part__Feature069007,Part__Feature069008,Part__Feature069009,Part__Feature069010,Part__Feature069011]
FEATURE [Part::Torus] Torus004
  Angle1 = -180
  Angle2 = 180
  Angle3 = 360
  AttacherType = Attacher::AttachEngine3D
  Placement = pos=(0,20,0) rot=(0,1,0;1.5708rad)
  Radius1 = 20
  Radius2 = 1.1
FEATURE [Part::Cylinder] Cylinder130  label="Cylinder188"
  Angle = 360
  AttacherType = Attacher::AttachEngine3D
  Height = 10
  Placement = pos=(0,4.67911,12.8558) rot=(-1,0,0;0.698132rad)
  Radius = 2.2
FEATURE [Part::Cone] Cone005
  Angle = 360
  AttacherType = Attacher::AttachEngine3D
  Height = 2
  Placement = pos=(0,3.71769,11.6141) rot=(-1,0,0;0.619592rad)
  Radius1 = 1.1
  Radius2 = 1.3
FEATURE [Part::Box] Box001027045025  label="Cube078"
  AttacherType = Attacher::AttachEngine3D
  Height = 22
  Length = 10
  Placement = pos=(-5,-4,0) rot=(0,0,1;0rad)
  Width = 24
FEATURE [Part::Box] Box001027045026  label="Cube079"
  AttacherType = Attacher::AttachEngine3D
  Height = 22
  Length = 10
  Placement = pos=(-5,0.461228,13.9369) rot=(-1,0,0;0.619592rad)
  Width = 24
FEATURE [Part::MultiCommon] Common056
  Shapes = -> [Torus004,Box001027045025]
FEATURE [Part::Cut] Cut071
  Base = -> Common056
  Tool = -> Box001027045026
FEATURE [Part::Cylinder] Cylinder131  label="Cylinder189"
  Angle = 360
  AttacherType = Attacher::AttachEngine3D
  Height = 6
  Placement = pos=(0,7.57166,16.303) rot=(-1,0,0;0.698132rad)
  Radius = 4
FEATURE [Part::MultiFuse] Fusion112044  label="torroidal-hole007"
  Placement = pos=(0,0,22) rot=(0,0,1;0rad)
  Shapes = -> [Cylinder130,Cone005,Cut071,Cylinder131]
FEATURE [Part::Torus] Torus005
  Angle1 = -180
  Angle2 = 180
  Angle3 = 360
  AttacherType = Attacher::AttachEngine3D
  Placement = pos=(0,20,0) rot=(0,1,0;1.5708rad)
  Radius1 = 20
  Radius2 = 1.1
FEATURE [Part::Cylinder] Cylinder132  label="Cylinder190"
  Angle = 360
  AttacherType = Attacher::AttachEngine3D
  Height = 10
  Placement = pos=(0,4.67911,12.8558) rot=(-1,0,0;0.698132rad)
  Radius = 2.2
FEATURE [Part::Cone] Cone006
  Angle = 360
  AttacherType = Attacher::AttachEngine3D
  Height = 2
  Placement = pos=(0,3.71769,11.6141) rot=(-1,0,0;0.619592rad)
  Radius1 = 1.1
  Radius2 = 1.3
FEATURE [Part::Box] Box001027045027  label="Cube080"
  AttacherType = Attacher::AttachEngine3D
  Height = 22
  Length = 10
  Placement = pos=(-5,-4,0) rot=(0,0,1;0rad)
  Width = 24
FEATURE [Part::Box] Box001027045028  label="Cube081"
  AttacherType = Attacher::AttachEngine3D
  Height = 22
  Length = 10
  Placement = pos=(-5,0.461228,13.9369) rot=(-1,0,0;0.619592rad)
  Width = 24
FEATURE [Part::MultiCommon] Common057
  Shapes = -> [Torus005,Box001027045027]
FEATURE [Part::Cut] Cut072
  Base = -> Common057
  Tool = -> Box001027045028
FEATURE [Part::Cylinder] Cylinder133  label="Cylinder191"
  Angle = 360
  AttacherType = Attacher::AttachEngine3D
  Height = 6
  Placement = pos=(0,7.57166,16.303) rot=(-1,0,0;0.698132rad)
  Radius = 4
FEATURE [Part::MultiFuse] Fusion112045  label="torroidal-hole008"
  Shapes = -> [Cylinder132,Cone006,Cut072,Cylinder133]
FEATURE [Part::Torus] Torus006
  Angle1 = -180
  Angle2 = 180
  Angle3 = 360
  AttacherType = Attacher::AttachEngine3D
  Placement = pos=(0,20,0) rot=(0,1,0;1.5708rad)
  Radius1 = 20
  Radius2 = 1.1
FEATURE [Part::Cylinder] Cylinder134  label="Cylinder192"
  Angle = 360
  AttacherType = Attacher::AttachEngine3D
  Height = 10
  Placement = pos=(0,4.67911,12.8558) rot=(-1,0,0;0.698132rad)
  Radius = 2.2
FEATURE [Part::Cone] Cone007
  Angle = 360
  AttacherType = Attacher::AttachEngine3D
  Height = 2
  Placement = pos=(0,3.71769,11.6141) rot=(-1,0,0;0.619592rad)
  Radius1 = 1.1
  Radius2 = 1.3
FEATURE [Part::Box] Box001027045029  label="Cube082"
  AttacherType = Attacher::AttachEngine3D
  Height = 22
  Length = 10
  Placement = pos=(-5,-4,0) rot=(0,0,1;0rad)
  Width = 24
FEATURE [Part::Box] Box001027045030  label="Cube083"
  AttacherType = Attacher::AttachEngine3D
  Height = 22
  Length = 10
  Placement = pos=(-5,0.461228,13.9369) rot=(-1,0,0;0.619592rad)
  Width = 24
FEATURE [Part::MultiCommon] Common058
  Shapes = -> [Torus006,Box001027045029]
FEATURE [Part::Cut] Cut073
  Base = -> Common058
  Tool = -> Box001027045030
FEATURE [Part::Cylinder] Cylinder135  label="Cylinder193"
  Angle = 360
  AttacherType = Attacher::AttachEngine3D
  Height = 6
  Placement = pos=(0,7.57166,16.303) rot=(-1,0,0;0.698132rad)
  Radius = 4
FEATURE [Part::MultiFuse] Fusion112046  label="torroidal-hole009"
  Placement = pos=(0,0,33) rot=(0,0,1;3.14159rad)
  Shapes = -> [Cylinder134,Cone007,Cut073,Cylinder135]
FEATURE [Part::Torus] Torus007
  Angle1 = -180
  Angle2 = 180
  Angle3 = 360
  AttacherType = Attacher::AttachEngine3D
  Placement = pos=(0,20,0) rot=(0,1,0;1.5708rad)
  Radius1 = 20
  Radius2 = 1.1
FEATURE [Part::Cylinder] Cylinder136  label="Cylinder194"
  Angle = 360
  AttacherType = Attacher::AttachEngine3D
  Height = 10
  Placement = pos=(0,4.67911,12.8558) rot=(-1,0,0;0.698132rad)
  Radius = 2.2
FEATURE [Part::Cone] Cone008
  Angle = 360
  AttacherType = Attacher::AttachEngine3D
  Height = 2
  Placement = pos=(0,3.71769,11.6141) rot=(-1,0,0;0.619592rad)
  Radius1 = 1.1
  Radius2 = 1.3
FEATURE [Part::Box] Box001027045031  label="Cube084"
  AttacherType = Attacher::AttachEngine3D
  Height = 22
  Length = 10
  Placement = pos=(-5,-4,0) rot=(0,0,1;0rad)
  Width = 24
FEATURE [Part::Box] Box001027045032  label="Cube085"
  AttacherType = Attacher::AttachEngine3D
  Height = 22
  Length = 10
  Placement = pos=(-5,0.461228,13.9369) rot=(-1,0,0;0.619592rad)
  Width = 24
FEATURE [Part::MultiCommon] Common059
  Shapes = -> [Torus007,Box001027045031]
FEATURE [Part::Cut] Cut074
  Base = -> Common059
  Tool = -> Box001027045032
FEATURE [Part::Cylinder] Cylinder137  label="Cylinder195"
  Angle = 360
  AttacherType = Attacher::AttachEngine3D
  Height = 6
  Placement = pos=(0,7.57166,16.303) rot=(-1,0,0;0.698132rad)
  Radius = 4
FEATURE [Part::MultiFuse] Fusion112047  label="torroidal-hole010"
  Placement = pos=(0,0,11) rot=(0,0,1;3.14159rad)
  Shapes = -> [Cylinder136,Cone008,Cut074,Cylinder137]
FEATURE [Part::Cone] Cone009
  Angle = 360
  AttacherType = Attacher::AttachEngine3D
  Height = 24
  Radius1 = 25
  Radius2 = 1
FEATURE [Part::Cone] Cone010
  Angle = 360
  AttacherType = Attacher::AttachEngine3D
  Height = 24
  Placement = pos=(0,0,3.11127) rot=(0,0,1;0rad)
  Radius1 = 25
  Radius2 = 1
FEATURE [Part::Cut] Cut075
  Base = -> Cone010
  Placement = pos=(0,0,-6.55567) rot=(0,0,1;0rad)
  Tool = -> Cone009
FEATURE [Part::Cone] Cone011
  Angle = 360
  AttacherType = Attacher::AttachEngine3D
  Height = 24
  Radius1 = 25
  Radius2 = 1
FEATURE [Part::Cone] Cone012
  Angle = 360
  AttacherType = Attacher::AttachEngine3D
  Height = 24
  Placement = pos=(0,0,3.11127) rot=(0,0,1;0rad)
  Radius1 = 25
  Radius2 = 1
FEATURE [Part::Cut] Cut076
  Base = -> Cone012
  Placement = pos=(0,0,-28.1113) rot=(0,0,1;0rad)
  Tool = -> Cone011
FEATURE [Part::Mirroring] Part__Mirroring007  label="Cut076 (Mirror #8)"
  Base = (0,0,0)
  Normal = (0,0,1)
  Placement = pos=(0,0,-21.5556) rot=(0,0,1;0rad)
  Source = -> Cut076
FEATURE [Part::MultiCommon] Common060
  Placement = pos=(0,20,0) rot=(0,1,0;1.5708rad)
  Shapes = -> [Cut075,Part__Mirroring007]
FEATURE [Part::Box] Box001027045033  label="Cube086"
  AttacherType = Attacher::AttachEngine3D
  Height = 22
  Length = 10
  Placement = pos=(-5,0.461228,13.9369) rot=(-1,0,0;0.619592rad)
  Width = 24
FEATURE [Part::Box] Box001027045034  label="Cube087"
  AttacherType = Attacher::AttachEngine3D
  Height = 22
  Length = 10
  Placement = pos=(-5,-4,0) rot=(0,0,1;0rad)
  Width = 24
FEATURE [Part::Cylinder] Cylinder138  label="Cylinder196"
  Angle = 360
  AttacherType = Attacher::AttachEngine3D
  Height = 6
  Placement = pos=(0,7.57166,16.303) rot=(-1,0,0;0.698132rad)
  Radius = 4
FEATURE [Part::Cone] Cone013
  Angle = 360
  AttacherType = Attacher::AttachEngine3D
  Height = 2
  Placement = pos=(0,3.71769,11.6141) rot=(-1,0,0;0.619592rad)
  Radius1 = 1.1
  Radius2 = 1.8
FEATURE [Part::Cylinder] Cylinder139  label="Cylinder197"
  Angle = 360
  AttacherType = Attacher::AttachEngine3D
  Height = 10
  Placement = pos=(0,4.67911,12.8558) rot=(-1,0,0;0.698132rad)
  Radius = 2.2
FEATURE [Part::Cut] Cut077
  Base = -> Box001027045034
  Tool = -> Box001027045033
FEATURE [Part::MultiCommon] Common061
  Shapes = -> [Cut077,Common060]
FEATURE [Part::MultiFuse] Fusion112048  label="lead-in-1"
  Shapes = -> [Cylinder138,Cone013,Cylinder139,Common061]
FEATURE [Part::Box] Box001027045035  label="Cube088"
  AttacherType = Attacher::AttachEngine3D
  Height = 61
  Length = 2.2
  Placement = pos=(0,-1.55563,-6) rot=(0,0,1;0.785398rad)
  Width = 2.2
FEATURE [Part::Feature] Part__Feature069012  label="tree-output-thread001"
  Placement = pos=(0,0,-10) rot=(0,0,1;0rad)
  shape: bbox 11.55 x 10 x 5.798 mm, 23 faces (baked)
FEATURE [Part::Cylinder] Cylinder140  label="base-thread-hole001"
  Angle = 360
  AttacherType = Attacher::AttachEngine3D
  Height = 6
  Placement = pos=(0,0,-10.5) rot=(0,0,1;0rad)
  Radius = 4
FEATURE [Part::Feature] Part__Feature069013  label="M6 thread009"
  Placement = pos=(0,7.89305,16.686) rot=(-1,0,0;0.698132rad)
  shape: bbox 11.55 x 10.62 x 10 mm, 23 faces (baked)
FEATURE [Part::Feature] Part__Feature069014  label="M6 thread010"
  Placement = pos=(0,-7.89305,27.686) rot=(0,-0.34202,0.939693;3.14159rad)
  shape: bbox 11.55 x 10.62 x 10 mm, 23 faces (baked)
FEATURE [Part::Feature] Part__Feature069015  label="M6 thread011"
  Placement = pos=(0,7.89305,38.686) rot=(-1,0,0;0.698132rad)
  shape: bbox 11.55 x 10.62 x 10 mm, 23 faces (baked)
FEATURE [Part::Feature] Part__Feature069016  label="M6 thread012"
  Placement = pos=(0,-7.89305,49.686) rot=(0,-0.34202,0.939693;3.14159rad)
  shape: bbox 11.55 x 10.62 x 10 mm, 23 faces (baked)
FEATURE [Part::Feature] Part__Feature069017  label="M6 thread013"
  Placement = pos=(0,7.89305,60.686) rot=(-1,0,0;0.698132rad)
  shape: bbox 11.55 x 10.62 x 10 mm, 23 faces (baked)
FEATURE [Part::Feature] Part__Feature069018  label="M6 thread014"
  Placement = pos=(0,-7.89305,71.686) rot=(0,-0.34202,0.939693;3.14159rad)
  shape: bbox 11.55 x 10.62 x 10 mm, 23 faces (baked)
FEATURE [Part::Cylinder] Cylinder141  label="Cylinder198"
  Angle = 360
  AttacherType = Attacher::AttachEngine3D
  Height = 26
  Placement = pos=(-8,0,-18) rot=(0,0,1;0rad)
  Radius = 1.7
FEATURE [Part::Cylinder] Cylinder142  label="Cylinder199"
  Angle = 360
  AttacherType = Attacher::AttachEngine3D
  Height = 26
  Placement = pos=(13,0,-18) rot=(0,0,1;0rad)
  Radius = 1.7
FEATURE [Part::Box] Box001027045036  label="Cube089"
  AttacherType = Attacher::AttachEngine3D
  Height = 2.7
  Length = 10
  Placement = pos=(9.5,-2.9,0) rot=(0,0,1;0rad)
  Width = 5.8
FEATURE [Part::Box] Box001027045037  label="Cube090"
  AttacherType = Attacher::AttachEngine3D
  Height = 2.7
  Length = 13.5
  Placement = pos=(-18,-2.9,0) rot=(0,0,1;0rad)
  Width = 5.8
FEATURE [Part::MultiFuse] Fusion112050  label="m3-nut-hole-005"
  Shapes = -> [Cylinder141,Box001027045037]
FEATURE [Part::MultiFuse] Fusion112051  label="m3-nut-hole-006"
  Shapes = -> [Box001027045036,Cylinder142]
FEATURE [Part::MultiFuse] Fusion112052  label="m3-nut-holes002"
  Placement = pos=(0,0,0) rot=(0,0,1;1.5708rad)
  Shapes = -> [Fusion112050,Fusion112051]
FEATURE [Part::Box] Box001027045038  label="Cube091"
  AttacherType = Attacher::AttachEngine3D
  Height = 90
  Length = 16
  Placement = pos=(-8,-16,-11) rot=(0,0,1;0rad)
  Width = 32
FEATURE [Part::Box] Box001027045039  label="Cube092"
  AttacherType = Attacher::AttachEngine3D
  Height = 30
  Length = 21
  Placement = pos=(-11,-16.5,27.4) rot=(1,0,0;0.698132rad)
  Width = 13
FEATURE [Part::Box] Box001027045040  label="Cube093"
  AttacherType = Attacher::AttachEngine3D
  Height = 30
  Length = 21
  Placement = pos=(11,16.5,38.4) rot=(0,0.34202,0.939693;3.14159rad)
  Width = 13
FEATURE [Part::Box] Box001027045041  label="Cube094"
  AttacherType = Attacher::AttachEngine3D
  Height = 30
  Length = 21
  Placement = pos=(11,16.5,60.4) rot=(0,0.34202,0.939693;3.14159rad)
  Width = 39
FEATURE [Part::Box] Box001027045042  label="Cube095"
  AttacherType = Attacher::AttachEngine3D
  Height = 30
  Length = 21
  Placement = pos=(11,16.5,16.4) rot=(0,0.34202,0.939693;3.14159rad)
  Width = 13
FEATURE [Part::Box] Box001027045043  label="Cube096"
  AttacherType = Attacher::AttachEngine3D
  Height = 30
  Length = 21
  Placement = pos=(-11,-16.5,49.4) rot=(1,0,0;0.698132rad)
  Width = 13
FEATURE [Part::Box] Box001027045044  label="Cube097"
  AttacherType = Attacher::AttachEngine3D
  Height = 30
  Length = 21
  Placement = pos=(-11,-16.5,71.4) rot=(1,0,0;0.698132rad)
  Width = 13
FEATURE [Part::MultiFuse] Fusion112054
  Shapes = -> [Box001027045041,Box001027045039,Box001027045040,Box001027045042,Box001027045043,Box001027045044]
FEATURE [Part::Cut] Cut078
  Base = -> Box001027045038
  Tool = -> Fusion112054
FEATURE [Part::Cylinder] Cylinder144  label="Cylinder201"
  Angle = 360
  AttacherType = Attacher::AttachEngine3D
  Height = 10
  Placement = pos=(-5,9,-11) rot=(0,0,1;0rad)
  Radius = 6
FEATURE [Part::MultiFuse] Fusion112055
  Shapes = -> [Cut078,Cylinder144]
FEATURE [Part::Cylinder] Cylinder145  label="Cylinder202"
  Angle = 360
  AttacherType = Attacher::AttachEngine3D
  Height = 21
  Placement = pos=(0,13,-11) rot=(0,0,1;0rad)
  Radius = 5
FEATURE [Part::MultiFuse] Fusion112056  label="body-blank001"
  Shapes = -> [Cylinder145,Fusion112055]
FEATURE [Part::MultiFuse] Fusion112057  label="M6-threads001"
  Shapes = -> [Part__Feature069013,Part__Feature069014,Part__Feature069015,Part__Feature069016,Part__Feature069017,Part__Feature069018]
FEATURE [Part::Cylinder] Cylinder146  label="PTFE-tube-hole"
  Angle = 360
  AttacherType = Attacher::AttachEngine3D
  Height = 9
  Placement = pos=(0,0,-12) rot=(0,0,1;0rad)
  Radius = 2.2
FEATURE [Part::Cone] Cone015
  Angle = 360
  AttacherType = Attacher::AttachEngine3D
  Height = 24
  Radius1 = 25
  Radius2 = 1
FEATURE [Part::Cone] Cone016
  Angle = 360
  AttacherType = Attacher::AttachEngine3D
  Height = 24
  Placement = pos=(0,0,3.11127) rot=(0,0,1;0rad)
  Radius1 = 25
  Radius2 = 1
FEATURE [Part::Cut] Cut079
  Base = -> Cone016
  Placement = pos=(0,0,-6.55567) rot=(0,0,1;0rad)
  Tool = -> Cone015
FEATURE [Part::Cone] Cone017
  Angle = 360
  AttacherType = Attacher::AttachEngine3D
  Height = 24
  Radius1 = 25
  Radius2 = 1
FEATURE [Part::Cone] Cone018
  Angle = 360
  AttacherType = Attacher::AttachEngine3D
  Height = 24
  Placement = pos=(0,0,3.11127) rot=(0,0,1;0rad)
  Radius1 = 25
  Radius2 = 1
FEATURE [Part::Cut] Cut080
  Base = -> Cone018
  Placement = pos=(0,0,-28.1113) rot=(0,0,1;0rad)
  Tool = -> Cone017
FEATURE [Part::Mirroring] Part__Mirroring008  label="Cut076 (Mirror #8)001"
  Base = (0,0,0)
  Normal = (0,0,1)
  Placement = pos=(0,0,-21.5556) rot=(0,0,1;0rad)
  Source = -> Cut080
FEATURE [Part::MultiCommon] Common062
  Placement = pos=(0,20,0) rot=(0,1,0;1.5708rad)
  Shapes = -> [Cut079,Part__Mirroring008]
FEATURE [Part::Box] Box001027045045  label="Cube098"
  AttacherType = Attacher::AttachEngine3D
  Height = 22
  Length = 10
  Placement = pos=(-5,0.461228,13.9369) rot=(-1,0,0;0.619592rad)
  Width = 24
FEATURE [Part::Box] Box001027045046  label="Cube099"
  AttacherType = Attacher::AttachEngine3D
  Height = 22
  Length = 10
  Placement = pos=(-5,-4,0) rot=(0,0,1;0rad)
  Width = 24
FEATURE [Part::Cylinder] Cylinder147  label="Cylinder204"
  Angle = 360
  AttacherType = Attacher::AttachEngine3D
  Height = 6
  Placement = pos=(0,7.57166,16.303) rot=(-1,0,0;0.698132rad)
  Radius = 4
FEATURE [Part::Cone] Cone019
  Angle = 360
  AttacherType = Attacher::AttachEngine3D
  Height = 2
  Placement = pos=(0,3.71769,11.6141) rot=(-1,0,0;0.619592rad)
  Radius1 = 1.1
  Radius2 = 1.8
FEATURE [Part::Cylinder] Cylinder148  label="Cylinder205"
  Angle = 360
  AttacherType = Attacher::AttachEngine3D
  Height = 10
  Placement = pos=(0,4.67911,12.8558) rot=(-1,0,0;0.698132rad)
  Radius = 2.2
FEATURE [Part::Cut] Cut081
  Base = -> Box001027045046
  Tool = -> Box001027045045
FEATURE [Part::MultiCommon] Common063
  Shapes = -> [Cut081,Common062]
FEATURE [Part::MultiFuse] Fusion112058  label="lead-in-002"
  Placement = pos=(0,0,22) rot=(0,0,1;0rad)
  Shapes = -> [Cylinder147,Cone019,Cylinder148,Common063]
FEATURE [Part::Cone] Cone020
  Angle = 360
  AttacherType = Attacher::AttachEngine3D
  Height = 24
  Radius1 = 25
  Radius2 = 1
FEATURE [Part::Cone] Cone021
  Angle = 360
  AttacherType = Attacher::AttachEngine3D
  Height = 24
  Placement = pos=(0,0,3.11127) rot=(0,0,1;0rad)
  Radius1 = 25
  Radius2 = 1
FEATURE [Part::Cut] Cut082
  Base = -> Cone021
  Placement = pos=(0,0,-6.55567) rot=(0,0,1;0rad)
  Tool = -> Cone020
FEATURE [Part::Cone] Cone022
  Angle = 360
  AttacherType = Attacher::AttachEngine3D
  Height = 24
  Radius1 = 25
  Radius2 = 1
FEATURE [Part::Cone] Cone023
  Angle = 360
  AttacherType = Attacher::AttachEngine3D
  Height = 24
  Placement = pos=(0,0,3.11127) rot=(0,0,1;0rad)
  Radius1 = 25
  Radius2 = 1
FEATURE [Part::Cut] Cut083
  Base = -> Cone023
  Placement = pos=(0,0,-28.1113) rot=(0,0,1;0rad)
  Tool = -> Cone022
FEATURE [Part::Mirroring] Part__Mirroring009  label="Cut076 (Mirror #8)002"
  Base = (0,0,0)
  Normal = (0,0,1)
  Placement = pos=(0,0,-21.5556) rot=(0,0,1;0rad)
  Source = -> Cut083
FEATURE [Part::MultiCommon] Common064
  Placement = pos=(0,20,0) rot=(0,1,0;1.5708rad)
  Shapes = -> [Cut082,Part__Mirroring009]
FEATURE [Part::Box] Box001027045047  label="Cube100"
  AttacherType = Attacher::AttachEngine3D
  Height = 22
  Length = 10
  Placement = pos=(-5,0.461228,13.9369) rot=(-1,0,0;0.619592rad)
  Width = 24
FEATURE [Part::Box] Box001027045048  label="Cube101"
  AttacherType = Attacher::AttachEngine3D
  Height = 22
  Length = 10
  Placement = pos=(-5,-4,0) rot=(0,0,1;0rad)
  Width = 24
FEATURE [Part::Cylinder] Cylinder149  label="Cylinder206"
  Angle = 360
  AttacherType = Attacher::AttachEngine3D
  Height = 6
  Placement = pos=(0,7.57166,16.303) rot=(-1,0,0;0.698132rad)
  Radius = 4
FEATURE [Part::Cone] Cone024
  Angle = 360
  AttacherType = Attacher::AttachEngine3D
  Height = 2
  Placement = pos=(0,3.71769,11.6141) rot=(-1,0,0;0.619592rad)
  Radius1 = 1.1
  Radius2 = 1.8
FEATURE [Part::Cylinder] Cylinder150  label="Cylinder207"
  Angle = 360
  AttacherType = Attacher::AttachEngine3D
  Height = 10
  Placement = pos=(0,4.67911,12.8558) rot=(-1,0,0;0.698132rad)
  Radius = 2.2
FEATURE [Part::Cut] Cut084
  Base = -> Box001027045048
  Tool = -> Box001027045047
FEATURE [Part::MultiCommon] Common065
  Shapes = -> [Cut084,Common064]
FEATURE [Part::MultiFuse] Fusion112059  label="lead-in-003"
  Placement = pos=(0,0,44) rot=(0,0,1;0rad)
  Shapes = -> [Cylinder149,Cone024,Cylinder150,Common065]
FEATURE [Part::Cone] Cone025
  Angle = 360
  AttacherType = Attacher::AttachEngine3D
  Height = 24
  Radius1 = 25
  Radius2 = 1
FEATURE [Part::Cone] Cone026
  Angle = 360
  AttacherType = Attacher::AttachEngine3D
  Height = 24
  Placement = pos=(0,0,3.11127) rot=(0,0,1;0rad)
  Radius1 = 25
  Radius2 = 1
FEATURE [Part::Cut] Cut085
  Base = -> Cone026
  Placement = pos=(0,0,-6.55567) rot=(0,0,1;0rad)
  Tool = -> Cone025
FEATURE [Part::Cone] Cone027
  Angle = 360
  AttacherType = Attacher::AttachEngine3D
  Height = 24
  Radius1 = 25
  Radius2 = 1
FEATURE [Part::Cone] Cone028
  Angle = 360
  AttacherType = Attacher::AttachEngine3D
  Height = 24
  Placement = pos=(0,0,3.11127) rot=(0,0,1;0rad)
  Radius1 = 25
  Radius2 = 1
FEATURE [Part::Cut] Cut086
  Base = -> Cone028
  Placement = pos=(0,0,-28.1113) rot=(0,0,1;0rad)
  Tool = -> Cone027
FEATURE [Part::Mirroring] Part__Mirroring010  label="Cut076 (Mirror #8)003"
  Base = (0,0,0)
  Normal = (0,0,1)
  Placement = pos=(0,0,-21.5556) rot=(0,0,1;0rad)
  Source = -> Cut086
FEATURE [Part::MultiCommon] Common066
  Placement = pos=(0,20,0) rot=(0,1,0;1.5708rad)
  Shapes = -> [Cut085,Part__Mirroring010]
FEATURE [Part::Box] Box001027045049  label="Cube102"
  AttacherType = Attacher::AttachEngine3D
  Height = 22
  Length = 10
  Placement = pos=(-5,0.461228,13.9369) rot=(-1,0,0;0.619592rad)
  Width = 24
FEATURE [Part::Box] Box001027045050  label="Cube103"
  AttacherType = Attacher::AttachEngine3D
  Height = 22
  Length = 10
  Placement = pos=(-5,-4,0) rot=(0,0,1;0rad)
  Width = 24
FEATURE [Part::Cylinder] Cylinder151  label="Cylinder208"
  Angle = 360
  AttacherType = Attacher::AttachEngine3D
  Height = 6
  Placement = pos=(0,7.57166,16.303) rot=(-1,0,0;0.698132rad)
  Radius = 4
FEATURE [Part::Cone] Cone029
  Angle = 360
  AttacherType = Attacher::AttachEngine3D
  Height = 2
  Placement = pos=(0,3.71769,11.6141) rot=(-1,0,0;0.619592rad)
  Radius1 = 1.1
  Radius2 = 1.8
FEATURE [Part::Cylinder] Cylinder152  label="Cylinder209"
  Angle = 360
  AttacherType = Attacher::AttachEngine3D
  Height = 10
  Placement = pos=(0,4.67911,12.8558) rot=(-1,0,0;0.698132rad)
  Radius = 2.2
FEATURE [Part::Cut] Cut087
  Base = -> Box001027045050
  Tool = -> Box001027045049
FEATURE [Part::MultiCommon] Common067
  Shapes = -> [Cut087,Common066]
FEATURE [Part::MultiFuse] Fusion112060  label="lead-in-004"
  Placement = pos=(0,0,11) rot=(0,0,1;3.14159rad)
  Shapes = -> [Cylinder151,Cone029,Cylinder152,Common067]
FEATURE [Part::Cone] Cone030
  Angle = 360
  AttacherType = Attacher::AttachEngine3D
  Height = 24
  Radius1 = 25
  Radius2 = 1
FEATURE [Part::Cone] Cone031
  Angle = 360
  AttacherType = Attacher::AttachEngine3D
  Height = 24
  Placement = pos=(0,0,3.11127) rot=(0,0,1;0rad)
  Radius1 = 25
  Radius2 = 1
FEATURE [Part::Cut] Cut088
  Base = -> Cone031
  Placement = pos=(0,0,-6.55567) rot=(0,0,1;0rad)
  Tool = -> Cone030
FEATURE [Part::Cone] Cone032
  Angle = 360
  AttacherType = Attacher::AttachEngine3D
  Height = 24
  Radius1 = 25
  Radius2 = 1
FEATURE [Part::Cone] Cone033
  Angle = 360
  AttacherType = Attacher::AttachEngine3D
  Height = 24
  Placement = pos=(0,0,3.11127) rot=(0,0,1;0rad)
  Radius1 = 25
  Radius2 = 1
FEATURE [Part::Cut] Cut089
  Base = -> Cone033
  Placement = pos=(0,0,-28.1113) rot=(0,0,1;0rad)
  Tool = -> Cone032
FEATURE [Part::Mirroring] Part__Mirroring011  label="Cut076 (Mirror #8)004"
  Base = (0,0,0)
  Normal = (0,0,1)
  Placement = pos=(0,0,-21.5556) rot=(0,0,1;0rad)
  Source = -> Cut089
FEATURE [Part::MultiCommon] Common068
  Placement = pos=(0,20,0) rot=(0,1,0;1.5708rad)
  Shapes = -> [Cut088,Part__Mirroring011]
FEATURE [Part::Box] Box001027045051  label="Cube104"
  AttacherType = Attacher::AttachEngine3D
  Height = 22
  Length = 10
  Placement = pos=(-5,0.461228,13.9369) rot=(-1,0,0;0.619592rad)
  Width = 24
FEATURE [Part::Box] Box001027045052  label="Cube105"
  AttacherType = Attacher::AttachEngine3D
  Height = 22
  Length = 10
  Placement = pos=(-5,-4,0) rot=(0,0,1;0rad)
  Width = 24
FEATURE [Part::Cylinder] Cylinder153  label="Cylinder210"
  Angle = 360
  AttacherType = Attacher::AttachEngine3D
  Height = 6
  Placement = pos=(0,7.57166,16.303) rot=(-1,0,0;0.698132rad)
  Radius = 4
FEATURE [Part::Cone] Cone034
  Angle = 360
  AttacherType = Attacher::AttachEngine3D
  Height = 2
  Placement = pos=(0,3.71769,11.6141) rot=(-1,0,0;0.619592rad)
  Radius1 = 1.1
  Radius2 = 1.8
FEATURE [Part::Cylinder] Cylinder154  label="Cylinder211"
  Angle = 360
  AttacherType = Attacher::AttachEngine3D
  Height = 10
  Placement = pos=(0,4.67911,12.8558) rot=(-1,0,0;0.698132rad)
  Radius = 2.2
FEATURE [Part::Cut] Cut090
  Base = -> Box001027045052
  Tool = -> Box001027045051
FEATURE [Part::MultiCommon] Common069
  Shapes = -> [Cut090,Common068]
FEATURE [Part::MultiFuse] Fusion112061  label="lead-in-005"
  Placement = pos=(0,0,33) rot=(0,0,1;3.14159rad)
  Shapes = -> [Cylinder153,Cone034,Cylinder154,Common069]
FEATURE [Part::Cone] Cone035
  Angle = 360
  AttacherType = Attacher::AttachEngine3D
  Height = 24
  Radius1 = 25
  Radius2 = 1
FEATURE [Part::Cone] Cone036
  Angle = 360
  AttacherType = Attacher::AttachEngine3D
  Height = 24
  Placement = pos=(0,0,3.11127) rot=(0,0,1;0rad)
  Radius1 = 25
  Radius2 = 1
FEATURE [Part::Cut] Cut091
  Base = -> Cone036
  Placement = pos=(0,0,-6.55567) rot=(0,0,1;0rad)
  Tool = -> Cone035
FEATURE [Part::Cone] Cone037
  Angle = 360
  AttacherType = Attacher::AttachEngine3D
  Height = 24
  Radius1 = 25
  Radius2 = 1
FEATURE [Part::Cone] Cone038
  Angle = 360
  AttacherType = Attacher::AttachEngine3D
  Height = 24
  Placement = pos=(0,0,3.11127) rot=(0,0,1;0rad)
  Radius1 = 25
  Radius2 = 1
FEATURE [Part::Cut] Cut092
  Base = -> Cone038
  Placement = pos=(0,0,-28.1113) rot=(0,0,1;0rad)
  Tool = -> Cone037
FEATURE [Part::Mirroring] Part__Mirroring012  label="Cut076 (Mirror #8)005"
  Base = (0,0,0)
  Normal = (0,0,1)
  Placement = pos=(0,0,-21.5556) rot=(0,0,1;0rad)
  Source = -> Cut092
FEATURE [Part::MultiCommon] Common070
  Placement = pos=(0,20,0) rot=(0,1,0;1.5708rad)
  Shapes = -> [Cut091,Part__Mirroring012]
FEATURE [Part::Box] Box001027045053  label="Cube106"
  AttacherType = Attacher::AttachEngine3D
  Height = 22
  Length = 10
  Placement = pos=(-5,0.461228,13.9369) rot=(-1,0,0;0.619592rad)
  Width = 24
FEATURE [Part::Box] Box001027045054  label="Cube107"
  AttacherType = Attacher::AttachEngine3D
  Height = 22
  Length = 10
  Placement = pos=(-5,-4,0) rot=(0,0,1;0rad)
  Width = 24
FEATURE [Part::Cylinder] Cylinder155  label="Cylinder212"
  Angle = 360
  AttacherType = Attacher::AttachEngine3D
  Height = 6
  Placement = pos=(0,7.57166,16.303) rot=(-1,0,0;0.698132rad)
  Radius = 4
FEATURE [Part::Cone] Cone039
  Angle = 360
  AttacherType = Attacher::AttachEngine3D
  Height = 2
  Placement = pos=(0,3.71769,11.6141) rot=(-1,0,0;0.619592rad)
  Radius1 = 1.1
  Radius2 = 1.8
FEATURE [Part::Cylinder] Cylinder156  label="Cylinder213"
  Angle = 360
  AttacherType = Attacher::AttachEngine3D
  Height = 10
  Placement = pos=(0,4.67911,12.8558) rot=(-1,0,0;0.698132rad)
  Radius = 2.2
FEATURE [Part::Cut] Cut093
  Base = -> Box001027045054
  Tool = -> Box001027045053
FEATURE [Part::MultiCommon] Common071
  Shapes = -> [Cut093,Common070]
FEATURE [Part::MultiFuse] Fusion112062  label="lead-in-006"
  Placement = pos=(0,0,55) rot=(0,0,1;3.14159rad)
  Shapes = -> [Cylinder155,Cone039,Cylinder156,Common071]
FEATURE [Part::MultiFuse] Fusion112063  label="all-lead-ins"
  Shapes = -> [Fusion112062,Fusion112059,Fusion112060,Fusion112058,Fusion112061,Fusion112048,Box001027045035]
FEATURE [Part::Cut] Cut094  label="blank-lead-ins"
  Base = -> Fusion112056
  Tool = -> Fusion112063
FEATURE [Part::Cylinder] Cylinder157  label="Cylinder214"
  Angle = 360
  AttacherType = Attacher::AttachEngine3D
  Height = 19
  Placement = pos=(0,12,21) rot=(-1,0,0;0.698132rad)
  Radius = 8
FEATURE [Part::Cylinder] Cylinder158  label="Cylinder215"
  Angle = 360
  AttacherType = Attacher::AttachEngine3D
  Height = 19
  Placement = pos=(0,12,21) rot=(-1,0,0;0.698132rad)
  Radius = 8
FEATURE [Part::Mirroring] Part__Mirroring013  label="Cylinder213 (Mirror #14)"
  Base = (0,0,0)
  Normal = (0,1,0)
  Placement = pos=(0,0,11) rot=(0,0,1;0rad)
  Source = -> Cylinder158
FEATURE [Part::MultiFuse] Fusion112065
  Placement = pos=(0,0,22) rot=(0,0,1;0rad)
  Shapes = -> [Cylinder157,Part__Mirroring013]
FEATURE [Part::MultiFuse] Fusion112066
  Shapes = -> [Cylinder157,Part__Mirroring013]
FEATURE [Part::MultiFuse] Fusion112067  label="pneumatic-nut-clearance"
  Shapes = -> [Fusion112066,Fusion112065]
FEATURE [Part::Cut] Cut098  label="m3-nut-2"
  Base = -> Cylinder064
  Placement = pos=(-5,9,47) rot=(0,0,1;3.14159rad)
  Tool = -> Fusion110
FEATURE [Part::MultiFuse] Fusion112068  label="threaded-blank"
  Shapes = -> [Fusion112057,Cut094]
FEATURE [Part::Cut] Cut099  label="blank-nut-clearance"
  Base = -> Fusion112068
  Tool = -> Fusion112067
FEATURE [Part::MultiFuse] Fusion112069  label="base-holes002"
  Shapes = -> [Fusion112052,Cut098]
FEATURE [Part::Cut] Cut100  label="final-blank"
  Base = -> Cut099
  Tool = -> Fusion112069
FEATURE [Part::Cut] Cut101  label="merger"
  Base = -> Cut100
  Tool = -> Cylinder146
FEATURE [Part::Feature] Part__Feature069019  label="M6 thread015"
  Placement = pos=(10.1005,0,27.5) rot=(0.92388,0,-0.382683;3.14159rad)
  shape: bbox 11.42 x 10 x 11.42 mm, 23 faces (baked)
FEATURE [Part::Cylinder] Cylinder161  label="M6-thread-hole"
  Angle = 360
  AttacherType = Attacher::AttachEngine3D
  Height = 6
  Placement = pos=(10.6,0,28) rot=(0.92388,0,-0.382683;3.14159rad)
  Radius = 4
FEATURE [Part::Cylinder] Cylinder171  label="M3-clear"
  Angle = 360
  AttacherType = Attacher::AttachEngine3D
  Height = 30
  Placement = pos=(7,13,15) rot=(1,0,0;1.5708rad)
  Radius = 1.75
FEATURE [Part::Cylinder] Cylinder172  label="M3-tap"
  Angle = 360
  AttacherType = Attacher::AttachEngine3D
  Height = 30
  Placement = pos=(7,13,15) rot=(1,0,0;1.5708rad)
  Radius = 1.4
FEATURE [Part::Cylinder] Cylinder186  label="M3-tap001"
  Angle = 360
  AttacherType = Attacher::AttachEngine3D
  Height = 30
  Placement = pos=(-6,13,27) rot=(1,0,0;1.5708rad)
  Radius = 1.4
FEATURE [Part::Cylinder] Cylinder188  label="screw-bump-bottom"
  Angle = 360
  AttacherType = Attacher::AttachEngine3D
  Height = 8
  Placement = pos=(-6,8,27) rot=(1,0,0;1.5708rad)
  Radius = 5
FEATURE [Part::Cylinder] Cylinder189  label="screw-bump-top"
  Angle = 360
  AttacherType = Attacher::AttachEngine3D
  Height = 8
  Placement = pos=(-6,0,-1) rot=(1,0,0;1.5708rad)
  Radius = 5
FEATURE [Part::Box] Box001027045132  label="Cube185"
  AttacherType = Attacher::AttachEngine3D
  Height = 18
  Length = 15
  Placement = pos=(-5,-5,-18) rot=(0,0,1;0rad)
  Width = 10
FEATURE [Part::Torus] Torus013
  Angle1 = -180
  Angle2 = 180
  Angle3 = 360
  AttacherType = Attacher::AttachEngine3D
  Placement = pos=(20,0,0) rot=(1,0,0;1.5708rad)
  Radius1 = 20
  Radius2 = 2.2
FEATURE [Part::Box] Box001027045133  label="Cube186"
  AttacherType = Attacher::AttachEngine3D
  Height = 32
  Length = 10
  Placement = pos=(0,-5,-22) rot=(0,0,1;0rad)
  Width = 10
FEATURE [Part::Cylinder] Cylinder190  label="Cylinder237"
  Angle = 360
  AttacherType = Attacher::AttachEngine3D
  Height = 32
  Placement = pos=(0,0,30) rot=(1,0,0;3.14159rad)
  Radius = 1.15
FEATURE [Part::Cylinder] Cylinder191  label="Cylinder238"
  Angle = 360
  AttacherType = Attacher::AttachEngine3D
  Height = 9
  Placement = pos=(0,0,4) rot=(1,0,0;3.14159rad)
  Radius = 2.2
FEATURE [Part::Cylinder] Cylinder192  label="Cylinder239"
  Angle = 360
  AttacherType = Attacher::AttachEngine3D
  Height = 17
  Placement = pos=(0,0,-15) rot=(0,0,1;0rad)
  Radius = 2.2
FEATURE [Part::Cylinder] Cylinder193  label="Cylinder240"
  Angle = 360
  AttacherType = Attacher::AttachEngine3D
  Height = 9
  Placement = pos=(0,0,33) rot=(1,0,0;3.14159rad)
  Radius = 2.2
FEATURE [Part::Box] Box001027045134  label="Cube187"
  AttacherType = Attacher::AttachEngine3D
  Height = 32
  Length = 10
  Placement = pos=(0,-5,-22) rot=(0,0,1;0rad)
  Width = 10
FEATURE [Part::Cut] Cut158
  Base = -> Cylinder192
  Placement = pos=(0,0,6) rot=(1,0,0;3.14159rad)
  Tool = -> Box001027045134
FEATURE [Part::Box] Box001027045135  label="Cube188"
  AttacherType = Attacher::AttachEngine3D
  Height = 25
  Length = 25
  Placement = pos=(-3,-5,-1) rot=(0,0,1;0rad)
  Width = 10
FEATURE [Part::MultiCommon] Common091
  Placement = pos=(5.85786,0,-14.1421) rot=(0,-1,0;0.785398rad)
  Shapes = -> [Torus013,Box001027045135]
FEATURE [Part::MultiCommon] Common089
  Shapes = -> [Common091,Box001027045132]
FEATURE [Part::MultiCommon] Common090
  Placement = pos=(0,0,4) rot=(1,0,0;3.14159rad)
  Shapes = -> [Common089,Box001027045133]
FEATURE [Part::MultiFuse] Fusion112082  label="filament-path001"
  Placement = pos=(0,0,5) rot=(0,0,1;0rad)
  Shapes = -> [Cylinder190,Cut158,Common090,Cylinder191,Cylinder193]
FEATURE [Part::Cylinder] Cylinder194  label="M3-clear001"
  Angle = 360
  AttacherType = Attacher::AttachEngine3D
  Height = 30
  Placement = pos=(-6,13,27) rot=(1,0,0;1.5708rad)
  Radius = 1.75
FEATURE [Part::Box] Box001027045136  label="Cube189"
  AttacherType = Attacher::AttachEngine3D
  Height = 28
  Length = 21
  Placement = pos=(-6,-8,5) rot=(0,0,1;0rad)
  Width = 16
FEATURE [Part::Chamfer] Chamfer015
  Base = -> Box001027045136
  Edges = 1 edges r=10: [Edge6]
FEATURE [Part::Chamfer] Chamfer016
  Base = -> Chamfer015
  Edges = 1 edges r=10: [Edge3]
FEATURE [Part::Cut] Cut159
  Base = -> Chamfer016
  Tool = -> Cylinder161
FEATURE [Part::MultiFuse] Fusion112083  label="body-a"
  Shapes = -> [Cut159,Part__Feature069019]
FEATURE [Part::MultiFuse] Fusion112084  label="body-b"
  Shapes = -> [Fusion112083,Cylinder188]
FEATURE [Part::MultiFuse] Fusion112085  label="body-ghost"
  Placement = pos=(0,0,-28) rot=(0,0,1;0rad)
  Shapes = -> [Fusion112083,Cylinder188]
FEATURE [Part::MultiFuse] Fusion112086  label="path-ghost"
  Placement = pos=(0,0,-23) rot=(0,0,1;0rad)
  Shapes = -> [Cylinder190,Cut158,Common090,Cylinder191,Cylinder193]
FEATURE [Part::Box] Box001027045137  label="Cube190"
  AttacherType = Attacher::AttachEngine3D
  Height = 28
  Length = 21
  Placement = pos=(-6,-8,-7) rot=(0,0,1;0rad)
  Width = 8
FEATURE [Part::Box] Box001027045138  label="Cube191"
  AttacherType = Attacher::AttachEngine3D
  Height = 28
  Length = 21
  Placement = pos=(-6,-9,-7) rot=(0,0,1;0rad)
  Width = 10
FEATURE [Part::Box] Box001027045139  label="Cube192"
  AttacherType = Attacher::AttachEngine3D
  Height = 28
  Length = 21
  Placement = pos=(-6,-9,21) rot=(0,1,0;0.785398rad)
  Width = 10
FEATURE [Part::MultiFuse] Fusion112087
  Placement = pos=(10,0,-17) rot=(0,0,1;0rad)
  Shapes = -> [Box001027045138,Box001027045139]
FEATURE [Part::Cut] Cut160
  Base = -> Box001027045137
  Tool = -> Fusion112087
FEATURE [Part::MultiFuse] Fusion112088  label="top-b"
  Shapes = -> [Cut160,Cylinder189]
FEATURE [Part::MultiFuse] Fusion112089  label="top-ghost"
  Placement = pos=(0,0,28) rot=(0,0,1;0rad)
  Shapes = -> [Cut160,Cylinder189]
FEATURE [Part::Cylinder] Cylinder195  label="M3-clear002"
  Angle = 360
  AttacherType = Attacher::AttachEngine3D
  Height = 30
  Placement = pos=(-6,13,-1) rot=(1,0,0;1.5708rad)
  Radius = 1.75
FEATURE [Part::Box] Box001027045140  label="Cube193"
  AttacherType = Attacher::AttachEngine3D
  Height = 6
  Length = 26
  Placement = pos=(-6,-4,2) rot=(0,0,1;0rad)
  Width = 21
FEATURE [Part::Cut] Cut161  label="top-c"
  Base = -> Fusion112088
  Tool = -> Box001027045140
FEATURE [Part::Cut] Cut162  label="top-c001"
  Base = -> Fusion112088
  Placement = pos=(0,0,28) rot=(0,0,1;0rad)
  Tool = -> Box001027045140
FEATURE [Part::Cut] Cut163  label="top-c002"
  Base = -> Fusion112088
  Placement = pos=(0,0,28) rot=(0,0,1;0rad)
  Tool = -> Box001027045140
FEATURE [Part::Cut] Cut164  label="top-c003"
  Base = -> Fusion112088
  Tool = -> Box001027045140
FEATURE [Part::Cut] Cut165  label="top-c004"
  Base = -> Fusion112088
  Tool = -> Box001027045140
FEATURE [Part::MultiFuse] Fusion112090
  Placement = pos=(0.2,0,0.2) rot=(0,0,1;0rad)
  Shapes = -> [Cut162,Cut164]
FEATURE [Part::MultiFuse] Fusion112091
  Placement = pos=(-0.2,0,-0.2) rot=(0,0,1;0rad)
  Shapes = -> [Cut165,Cut163]
FEATURE [Part::MultiFuse] Fusion112092  label="offset-tops"
  Shapes = -> [Fusion112091,Fusion112090]
FEATURE [Part::Cut] Cut166  label="body-c"
  Base = -> Fusion112084
  Tool = -> Fusion112092
FEATURE [Part::MultiFuse] Fusion112093  label="top-m3-clear"
  Shapes = -> [Cylinder195,Cylinder171]
FEATURE [Part::Cut] Cut167  label="top-d"
  Base = -> Cut161
  Tool = -> Fusion112093
FEATURE [Part::MultiFuse] Fusion112094  label="m3-taps"
  Shapes = -> [Cylinder172,Cylinder186]
FEATURE [Part::Cut] Cut168  label="body-d"
  Base = -> Cut166
  Tool = -> Fusion112094
FEATURE [Part::MultiFuse] Fusion112095  label="filament-path002"
  Placement = pos=(0,0,5) rot=(0,0,1;0rad)
  Shapes = -> [Cylinder190,Cut158,Common090,Cylinder191,Cylinder193]
FEATURE [Part::Cut] Cut169  label="base"
  Base = -> Cut168
  Tool = -> Fusion112082
FEATURE [Part::MultiFuse] Fusion112096  label="top-path"
  Shapes = -> [Fusion112086,Fusion112095]
FEATURE [Part::Cut] Cut170  label="top"
  Base = -> Cut167
  Tool = -> Fusion112096
FEATURE [Part::Cylinder] Cylinder196  label="Cylinder241"
  Angle = 360
  AttacherType = Attacher::AttachEngine3D
  Height = 20
  Placement = pos=(0,0,-74) rot=(0,0,1;0rad)
  Radius = 4
FEATURE [Part::Box] Box001027045141  label="Cube194"
  AttacherType = Attacher::AttachEngine3D
  Height = 25
  Length = 10
  Placement = pos=(3,-5,-77) rot=(0,0,1;0rad)
  Width = 10
FEATURE [Part::Feature] Box001027045142
  Placement = pos=(5.83013,0.0980762,-77) rot=(0,0,1;1.0472rad)
  shape: bbox 13.66 x 13.66 x 25 mm, 6 faces (baked)
FEATURE [Part::Feature] Box001027045143
  Placement = pos=(2.83013,5.09808,-77) rot=(0,0,1;2.0944rad)
  shape: bbox 13.66 x 13.66 x 25 mm, 6 faces (baked)
FEATURE [Part::Feature] Box001027045144
  Placement = pos=(-3,5,-77) rot=(0,0,1;3.14159rad)
  shape: bbox 10 x 10 x 25 mm, 6 faces (baked)
FEATURE [Part::Feature] Box001027045145
  Placement = pos=(-5.83013,-0.0980762,-77) rot=(0,0,1;4.18879rad)
  shape: bbox 13.66 x 13.66 x 25 mm, 6 faces (baked)
FEATURE [Part::Feature] Box001027045146
  Placement = pos=(-2.83013,-5.09808,-77) rot=(0,0,-1;1.0472rad)
  shape: bbox 13.66 x 13.66 x 25 mm, 6 faces (baked)
FEATURE [Part::MultiFuse] Fusion112097
  Shapes = -> [Box001027045141,Box001027045142,Box001027045145,Box001027045144,Box001027045143,Box001027045146]
FEATURE [Part::Cut] Cut171  label="m3-nut-003"
  Base = -> Cylinder196
  Tool = -> Fusion112097
FEATURE [App::DocumentObjectGroup] Group003  label="Useful Primitives"
  Group = -> [Part__Feature069012,Cylinder140,Cylinder194,Fusion087,Fusion086,Part__Feature068,Fusion099,Fusion100,Cut171,Cylinder097]
FEATURE [Part::Box] Box001027045147  label="Cube195"
  AttacherType = Attacher::AttachEngine3D
  Height = 43
  Length = 23
  Placement = pos=(52,-8.8,-59) rot=(0,0,1;0rad)
  Width = 4
FEATURE [Part::Box] Box001027045148  label="Cube196"
  AttacherType = Attacher::AttachEngine3D
  Height = 26
  Length = 29
  Placement = pos=(23,-2,-64) rot=(0,0,1;0rad)
  Width = 10
FEATURE [Part::Box] Box001027045149  label="Cube197"
  AttacherType = Attacher::AttachEngine3D
  Height = 15
  Length = 79
  Placement = pos=(-4,-8.8,-64) rot=(0,0,1;0rad)
  Width = 13
FEATURE [Part::Cut] Cut172
  Base = -> Box001027011
  Tool = -> Box001027045148
FEATURE [Part::Cut] Cut030  label="cut-lever-block"
  Base = -> Cut029
  Placement = pos=(0,0,-6) rot=(0,0,1;0rad)
  Tool = -> Cylinder060
FEATURE [App::DocumentObjectGroup] Group001  label="Guillotine"
  Group = -> [Cut002,Fusion048,Part__Feature035,Part__Feature066,Cylinder013,Part__Feature067,Cut004,Cut030,Cylinder069,Cut057,Chamfer011,Chamfer014,Cut063]
FEATURE [Part::Cylinder] Cylinder197  label="rocker-cut001"
  Angle = 360
  AttacherType = Attacher::AttachEngine3D
  Height = 18
  Placement = pos=(0,7,-58) rot=(1,0,0;1.5708rad)
  Radius = 4.2
FEATURE [Part::Box] Box001027045150  label="Cube198"
  AttacherType = Attacher::AttachEngine3D
  Height = 15
  Length = 20
  Placement = pos=(-14,-11.8,-72) rot=(0,0,1;0rad)
  Width = 18
FEATURE [Part::MultiFuse] Fusion112098
  Shapes = -> [Box001027045150,Cylinder197]
FEATURE [Part::Cut] Cut173
  Base = -> Box001027045149
  Tool = -> Fusion112098
FEATURE [Part::Chamfer] Chamfer017
  Base = -> Cut173
  Edges = 1 edges r=2: [Edge4]
FEATURE [Part::Box] Box001027045151  label="Cube199"
  AttacherType = Attacher::AttachEngine3D
  Height = 43
  Length = 41
  Placement = pos=(35,0,-59) rot=(0,0,1;0rad)
  Width = 7
FEATURE [Part::Box] Box001027045152  label="Cube200"
  AttacherType = Attacher::AttachEngine3D
  Height = 43
  Length = 25
  Placement = pos=(52,-10.6,-59) rot=(0,0,1;0rad)
  Width = 6
FEATURE [Part::Box] Box001027045153  label="Cube201"
  AttacherType = Attacher::AttachEngine3D
  Height = 26
  Length = 29
  Placement = pos=(23,-2,-64) rot=(0,0,1;0rad)
  Width = 10
FEATURE [Part::Cut] Cut174
  Base = -> Box001027045151
  Tool = -> Box001027045153
FEATURE [Part::MultiFuse] Fusion112099
  Shapes = -> [Box001027045152,Cut174]
FEATURE [Part::Cut] Cut175
  Base = -> Chamfer017
  Tool = -> Fusion112099
FEATURE [Part::Cylinder] Cylinder198  label="Cylinder242"
  Angle = 360
  AttacherType = Attacher::AttachEngine3D
  Height = 20
  Placement = pos=(56,8,-54) rot=(1,0,0;1.5708rad)
  Radius = 1.7
FEATURE [Part::Cylinder] Cylinder199  label="Cylinder243"
  Angle = 360
  AttacherType = Attacher::AttachEngine3D
  Height = 20
  Placement = pos=(71,8,-54) rot=(1,0,0;1.5708rad)
  Radius = 1.7
FEATURE [Part::Cylinder] Cylinder200  label="Cylinder244"
  Angle = 360
  AttacherType = Attacher::AttachEngine3D
  Height = 20
  Placement = pos=(56,8,-54) rot=(1,0,0;1.5708rad)
  Radius = 1.7
FEATURE [Part::Cylinder] Cylinder201  label="Cylinder245"
  Angle = 360
  AttacherType = Attacher::AttachEngine3D
  Height = 20
  Placement = pos=(71,8,-54) rot=(1,0,0;1.5708rad)
  Radius = 1.7
FEATURE [Part::Cylinder] Cylinder202  label="Cylinder246"
  Angle = 360
  AttacherType = Attacher::AttachEngine3D
  Height = 20
  Placement = pos=(56,8,-54) rot=(1,0,0;1.5708rad)
  Radius = 1.4
FEATURE [Part::Cylinder] Cylinder203  label="Cylinder247"
  Angle = 360
  AttacherType = Attacher::AttachEngine3D
  Height = 20
  Placement = pos=(71,8,-54) rot=(1,0,0;1.5708rad)
  Radius = 1.4
FEATURE [Part::MultiFuse] Fusion112100
  Placement = pos=(0,0,1) rot=(0,0,1;0rad)
  Shapes = -> [Cylinder198,Cylinder199]
FEATURE [Part::MultiFuse] Fusion112101
  Placement = pos=(0,0,1) rot=(0,0,1;0rad)
  Shapes = -> [Cylinder200,Cylinder201]
FEATURE [Part::MultiFuse] Fusion112102
  Placement = pos=(0,0,1) rot=(0,0,1;0rad)
  Shapes = -> [Cylinder202,Cylinder203]
FEATURE [Part::Cut] Cut176
  Base = -> Cut175
  Tool = -> Fusion112100
FEATURE [Part::Cut] Cut177
  Base = -> Box001027045147
  Tool = -> Fusion112101
FEATURE [Part::Cut] Cut178
  Base = -> Cut172
  Tool = -> Fusion112102
FEATURE [Part::Cylinder] Cylinder204  label="Cylinder248"
  Angle = 360
  AttacherType = Attacher::AttachEngine3D
  Height = 20
  Placement = pos=(26,8,-54) rot=(1,0,0;1.5708rad)
  Radius = 1.7
FEATURE [Part::Cylinder] Cylinder205  label="Cylinder249"
  Angle = 360
  AttacherType = Attacher::AttachEngine3D
  Height = 20
  Placement = pos=(46,8,-54) rot=(1,0,0;1.5708rad)
  Radius = 1.7
FEATURE [Part::MultiFuse] Fusion112103
  Placement = pos=(0,0,-2) rot=(0,0,1;0rad)
  Shapes = -> [Cylinder204,Cylinder205]
FEATURE [Part::Cut] Cut179
  Base = -> Cut176
  Tool = -> Fusion112103
FEATURE [Part::Box] Box001027045154  label="Cube202"
  AttacherType = Attacher::AttachEngine3D
  Height = 24
  Length = 47
  Placement = pos=(-5,-4.5,-34) rot=(0,1,0;0rad)
  Width = 4.5
FEATURE [Part::Box] Box001027045155  label="Cube203"
  AttacherType = Attacher::AttachEngine3D
  Height = 12
  Length = 16
  Placement = pos=(-5,0,-22) rot=(0,1,0;0rad)
  Width = 4.5
FEATURE [Part::Box] Box001027045156  label="Cube204"
  AttacherType = Attacher::AttachEngine3D
  Height = 10
  Length = 21
  Placement = pos=(20,-2.5,-42) rot=(0,0,1;0rad)
  Width = 9.5
FEATURE [Part::Chamfer] Chamfer018
  Base = -> Box001027045156
  Edges = 2 edges r=5: [Edge2,Edge6]
FEATURE [Part::Fillet] Fillet026  label="adjuster-block"
  Base = -> Chamfer018
  Edges = 2 edges r=3: [Edge10,Edge18]
  Placement = pos=(-11,-2,7) rot=(0,0,1;0rad)
FEATURE [Part::Cylinder] Cylinder208  label="Cylinder252"
  Angle = 360
  AttacherType = Attacher::AttachEngine3D
  Height = 30
  Placement = pos=(19.5,2,-45) rot=(0,0,1;0rad)
  Radius = 1.4
FEATURE [Part::Box] Box001027045157  label="Cube205"
  AttacherType = Attacher::AttachEngine3D
  Height = 18
  Length = 40
  Placement = pos=(15,0.2,-34) rot=(0,0,1;0rad)
  Width = 4
FEATURE [Part::MultiFuse] Fusion112104
  Shapes = -> [Cut178,Box001027045157]
FEATURE [Part::Chamfer] Chamfer019
  Base = -> Fusion112104
  Edges = 1 edges r=3.9: [Edge12]
FEATURE [Part::Chamfer] Chamfer020
  Base = -> Chamfer019
  Edges = 1 edges r=10.5: [Edge31]
FEATURE [Part::Cut] Cut180
  Base = -> Chamfer020
  Tool = -> Fillet025
FEATURE [Part::Box] Box001027045158  label="Cube206"
  AttacherType = Attacher::AttachEngine3D
  Height = 10
  Length = 33
  Placement = pos=(0,-7,-44) rot=(0,0,1;0rad)
  Width = 16
FEATURE [Part::Cut] Cut181
  Base = -> Fillet026
  Tool = -> Box001027045158
FEATURE [Part::Box] Box001027045159  label="Cube207"
  AttacherType = Attacher::AttachEngine3D
  Height = 10
  Length = 20
  Placement = pos=(29,-6,-9) rot=(0,1,0;0.139626rad)
  Width = 10
FEATURE [Part::Cylinder] Cylinder209  label="Cylinder253"
  Angle = 360
  AttacherType = Attacher::AttachEngine3D
  Height = 30
  Placement = pos=(19.5,2,-70) rot=(0,0,1;0rad)
  Radius = 2.5
FEATURE [Part::Cut] Cut183
  Base = -> Cut181
  Tool = -> Cylinder208
FEATURE [Part::Box] Box001027045160  label="Cube208"
  AttacherType = Attacher::AttachEngine3D
  Height = 21
  Length = 5
  Placement = pos=(17,2,-68) rot=(0,0,1;0rad)
  Width = 10
FEATURE [Part::MultiFuse] Fusion112106
  Shapes = -> [Cylinder209,Box001027045160]
FEATURE [Part::Cut] Cut184
  Base = -> Cut179
  Tool = -> Fusion112106
FEATURE [Part::Cylinder] Cylinder210  label="cutter-fit-cylinder001"
  Angle = 360
  AttacherType = Attacher::AttachEngine3D
  Height = 21
  Placement = pos=(45,5,-26) rot=(1,0,0;1.5708rad)
  Radius = 3.2
FEATURE [Part::Cut] Cut186
  Base = -> Cut180
  Tool = -> Cylinder074
FEATURE [Part::Box] Box001027045161  label="Cube209"
  AttacherType = Attacher::AttachEngine3D
  Height = 15
  Length = 30
  Placement = pos=(-10,-7,-57) rot=(0,0,1;0rad)
  Width = 15
FEATURE [Part::Box] Box001027045162  label="Cube210"
  AttacherType = Attacher::AttachEngine3D
  Height = 16
  Length = 17
  Placement = pos=(0,-8,-36) rot=(0,0,1;0rad)
  Width = 18
FEATURE [Part::Cut] Cut188  label="adjust-block"
  Base = -> Cut183
  Tool = -> Box001027045162
FEATURE [Part::Feature] Part__Feature069020  label="M6 thread016"
  Placement = pos=(45,-4,-26) rot=(0.935113,0.250563,-0.250563;1.63783rad)
  shape: bbox 10 x 5.798 x 11.55 mm, 23 faces (baked)
FEATURE [Part::Feature] Part__Feature069021  label="M6 thread017"
  Placement = pos=(45,-4,-26) rot=(0.935113,0.250563,-0.250563;1.63783rad)
  shape: bbox 10 x 5.798 x 11.55 mm, 23 faces (baked)
FEATURE [Part::Mirroring] Part__Mirroring014  label="M6 thread017 (Mirror #14)"
  Base = (0,0,0)
  Normal = (0,1,0)
  Source = -> Part__Feature069021
FEATURE [Part::MultiFuse] Fusion112109
  Shapes = -> [Cut186,Part__Mirroring014]
FEATURE [Part::Cylinder] Cylinder211  label="Cylinder254"
  Angle = 360
  AttacherType = Attacher::AttachEngine3D
  Height = 74
  Placement = pos=(0,0,-62) rot=(0,0,1;0rad)
  Radius = 2
FEATURE [Part::Box] Box001027045163  label="Cube211"
  AttacherType = Attacher::AttachEngine3D
  Height = 60
  Length = 10
  Placement = pos=(-10,-2,-57) rot=(0,0,1;0rad)
  Width = 4
FEATURE [Part::MultiFuse] Fusion112110
  Placement = pos=(2.5,0,0) rot=(0,0,1;0rad)
  Shapes = -> [Cylinder211,Box001027045163]
FEATURE [Part::Cut] Cut189  label="base-and-mount-b"
  Base = -> Cut184
  Tool = -> Fusion112110
FEATURE [Part::MultiFuse] Fusion112112  label="move-arm-1"
  Shapes = -> [Box001027033,Box001027045154]
FEATURE [Part::Cut] Cut190  label="move-arm-2"
  Base = -> Fusion112112
  Tool = -> Box001027045159
FEATURE [Part::Cut] Cut191  label="move-arm-3"
  Base = -> Cut190
  Tool = -> Cylinder210
FEATURE [Part::MultiFuse] Fusion112113  label="move-arm-4"
  Shapes = -> [Cut191,Part__Feature069020]
FEATURE [Part::Cylinder] Cylinder214  label="bearing-fit-cylinder001"
  Angle = 360
  AttacherType = Attacher::AttachEngine3D
  Height = 21
  Placement = pos=(64,5,-31) rot=(1,0,0;1.5708rad)
  Radius = 4.6
FEATURE [Part::Cut] Cut192  label="move-arm-5"
  Base = -> Fusion112113
  Placement = pos=(-6.44714,0,-21.2943) rot=(0,-1,0;0.314159rad)
  Tool = -> Cylinder214
FEATURE [Part::Cut] Cut193  label="move-arm-6"
  Base = -> Cut192
  Placement = pos=(12.7119,0,18.2598) rot=(0,1,0;0.314159rad)
  Tool = -> Box001027045161
FEATURE [Part::Box] Box001027045164  label="Cube212"
  AttacherType = Attacher::AttachEngine3D
  Height = 60
  Length = 10
  Placement = pos=(-10,-2,-57) rot=(0,0,1;0rad)
  Width = 4
FEATURE [Part::Cylinder] Cylinder215  label="Cylinder255"
  Angle = 360
  AttacherType = Attacher::AttachEngine3D
  Height = 74
  Placement = pos=(0,0,-62) rot=(0,0,1;0rad)
  Radius = 2
FEATURE [Part::MultiFuse] Fusion112115  label="top-slot-1"
  Placement = pos=(2.5,0,0) rot=(0,0,1;0rad)
  Shapes = -> [Cylinder215,Box001027045164]
FEATURE [Part::Box] Box001027045165  label="Cube213"
  AttacherType = Attacher::AttachEngine3D
  Height = 60
  Length = 10
  Placement = pos=(-10,-2,-57) rot=(0,0,1;0rad)
  Width = 4
FEATURE [Part::Cylinder] Cylinder216  label="Cylinder256"
  Angle = 360
  AttacherType = Attacher::AttachEngine3D
  Height = 74
  Placement = pos=(0,0,-62) rot=(0,0,1;0rad)
  Radius = 2
FEATURE [Part::MultiFuse] Fusion112116  label="top-slot-002"
  Placement = pos=(2.5,0,0) rot=(0,0,1;0rad)
  Shapes = -> [Cylinder216,Box001027045165]
FEATURE [Part::Cut] Cut196  label="top-slot-half-1"
  Base = -> Box001027045155
  Tool = -> Fusion112116
FEATURE [Part::Cylinder] Cylinder217  label="rocker-cut002"
  Angle = 360
  AttacherType = Attacher::AttachEngine3D
  Height = 18
  Placement = pos=(0,9,-8) rot=(1,0,0;1.5708rad)
  Radius = 4.2
FEATURE [Part::Cut] Cut197  label="top-slot-half-2"
  Base = -> Cut196
  Tool = -> Cylinder217
FEATURE [Part::Cylinder] Cylinder218  label="Cylinder257"
  Angle = 360
  AttacherType = Attacher::AttachEngine3D
  Height = 20
  Placement = pos=(7,11,-19) rot=(1,0,0;1.5708rad)
  Radius = 1.7
FEATURE [Part::Cylinder] Cylinder219  label="Cylinder258"
  Angle = 360
  AttacherType = Attacher::AttachEngine3D
  Height = 20
  Placement = pos=(7,11,-13) rot=(1,0,0;1.5708rad)
  Radius = 1.7
FEATURE [Part::Cylinder] Cylinder220  label="Cylinder259"
  Angle = 360
  AttacherType = Attacher::AttachEngine3D
  Height = 20
  Placement = pos=(7,11,-19) rot=(1,0,0;1.5708rad)
  Radius = 1.4
FEATURE [Part::Cylinder] Cylinder221  label="Cylinder260"
  Angle = 360
  AttacherType = Attacher::AttachEngine3D
  Height = 20
  Placement = pos=(7,11,-13) rot=(1,0,0;1.5708rad)
  Radius = 1.4
FEATURE [Part::MultiFuse] Fusion112117  label="top-slot-m3-clearance"
  Shapes = -> [Cylinder218,Cylinder219]
FEATURE [Part::MultiFuse] Fusion112118  label="top-slot-m3-tap"
  Shapes = -> [Cylinder220,Cylinder221]
FEATURE [Part::Cut] Cut198  label="top-slot-plate-2"
  Base = -> Cut197
  Tool = -> Fusion112117
FEATURE [Part::Cylinder] Cylinder222  label="bearing-fit-cylinder002"
  Angle = 360
  AttacherType = Attacher::AttachEngine3D
  Height = 21
  Placement = pos=(64,5,-31) rot=(1,0,0;1.5708rad)
  Radius = 1.7
FEATURE [Part::Cylinder] Cylinder223  label="bearing-fit-cylinder003"
  Angle = 360
  AttacherType = Attacher::AttachEngine3D
  Height = 21
  Placement = pos=(64,5,-31) rot=(1,0,0;1.5708rad)
  Radius = 1.7
FEATURE [Part::Cut] Cut200
  Base = -> Fusion112109
  Tool = -> Cylinder222
FEATURE [Part::Cut] Cut201
  Base = -> Cut177
  Tool = -> Cylinder223
FEATURE [App::DocumentObjectGroup] Group  label="legacy"
  Group = -> [Cut039,Cut041,Chamfer004,Fusion085,Cut101,Fusion112085,Fusion112089,Cut169,Cut170,Torus001,Part__Feature070,Cylinder112,Fusion112022,Fusion112033,Fusion112043,Cylinder119,Fusion112036,Fusion112045,Fusion112047,Fusion112044,Fusion112046,Fusion112027,Cylinder122,Fusion112028,Cut188,Fusion091,Cylinder077,Box001027016,Fusion107,Box001027014,Fusion112104,Cut200,Cut201,Group001,Cut189]
FEATURE [Part::Fillet] Fillet032  label="top-slot-plate"
  Base = -> Cut198
  Edges = 1 edges r=7: [Edge3]
FEATURE [Part::Fillet] Fillet033
  Base = -> Cut200
  Edges = 1 edges r=15: [Edge111]
FEATURE [Part::Fillet] Fillet034
  Base = -> Cut201
  Edges = 1 edges r=15: [Edge12]
FEATURE [Part::Fillet] Fillet035
  Base = -> Fillet033
  Edges = 2 edges r=2.5: [Edge63,Edge65]
FEATURE [Part::Fillet] Fillet038  label="bearing-support-1a"
  Base = -> Fillet034
  Edges = 1 edges r=6: [Edge17]
FEATURE [Part::Fillet] Fillet039  label="bearing-support-2a"
  Base = -> Fillet035
  Edges = 1 edges r=10: [Edge65]
FEATURE [Part::Box] Box001027045166  label="Cube214"
  AttacherType = Attacher::AttachEngine3D
  Height = 35
  Length = 46
  Placement = pos=(-7,-7,-36) rot=(0,0,1;0rad)
  Width = 32
FEATURE [Part::Box] Box001027045167  label="Cube215"
  AttacherType = Attacher::AttachEngine3D
  Height = 44
  Length = 12
  Placement = pos=(28,-2.25,-41) rot=(0,0,1;0rad)
  Width = 31
FEATURE [Part::Cut] Cut202
  Base = -> Box001027045166
  Tool = -> Box001027045167
FEATURE [Part::Box] Box001027045168  label="Cube216"
  AttacherType = Attacher::AttachEngine3D
  Height = 25
  Length = 40
  Placement = pos=(32,-4.5,-33) rot=(0,1,0;0.366519rad)
  Width = 4.5
FEATURE [Part::Box] Box001027045169  label="Cube217"
  AttacherType = Attacher::AttachEngine3D
  Height = 24
  Length = 47
  Placement = pos=(-5,-4.5,-34) rot=(0,1,0;0rad)
  Width = 4.5
FEATURE [Part::Box] Box001027045170  label="Cube218"
  AttacherType = Attacher::AttachEngine3D
  Height = 10
  Length = 20
  Placement = pos=(29,-6,-9) rot=(0,1,0;0.139626rad)
  Width = 10
FEATURE [Part::Cylinder] Cylinder224  label="cutter-fit-cylinder002"
  Angle = 360
  AttacherType = Attacher::AttachEngine3D
  Height = 21
  Placement = pos=(45,5,-26) rot=(1,0,0;1.5708rad)
  Radius = 3.2
FEATURE [Part::Box] Box001027045171  label="Cube219"
  AttacherType = Attacher::AttachEngine3D
  Height = 15
  Length = 30
  Placement = pos=(-10,-7,-57) rot=(0,0,1;0rad)
  Width = 15
FEATURE [Part::Feature] Part__Feature069022  label="M6 thread018"
  Placement = pos=(45,-4,-26) rot=(0.935113,0.250563,-0.250563;1.63783rad)
  shape: bbox 10 x 5.798 x 11.55 mm, 23 faces (baked)
FEATURE [Part::MultiFuse] Fusion112119  label="move-arm-007"
  Shapes = -> [Box001027045168,Box001027045169]
FEATURE [Part::Cut] Cut203  label="move-arm-008"
  Base = -> Fusion112119
  Tool = -> Box001027045170
FEATURE [Part::Cut] Cut204  label="move-arm-009"
  Base = -> Cut203
  Tool = -> Cylinder224
FEATURE [Part::MultiFuse] Fusion112120  label="move-arm-010"
  Shapes = -> [Cut204,Part__Feature069022]
FEATURE [Part::Cylinder] Cylinder225  label="bearing-fit-cylinder004"
  Angle = 360
  AttacherType = Attacher::AttachEngine3D
  Height = 21
  Placement = pos=(64,5,-31) rot=(1,0,0;1.5708rad)
  Radius = 4.6
FEATURE [Part::Cut] Cut205  label="move-arm-011"
  Base = -> Fusion112120
  Placement = pos=(-6.44714,0,-21.2943) rot=(0,-1,0;0.314159rad)
  Tool = -> Cylinder225
FEATURE [Part::Cut] Cut206  label="move-arm-012"
  Base = -> Cut205
  Placement = pos=(12.7119,0,18.2598) rot=(0,1,0;0.314159rad)
  Tool = -> Box001027045171
FEATURE [Part::Box] Box001027045172  label="Cube220"
  AttacherType = Attacher::AttachEngine3D
  Height = 35
  Length = 46
  Placement = pos=(-7,-7,-36) rot=(0,0,1;0rad)
  Width = 32
FEATURE [Part::Box] Box001027045173  label="Cube221"
  AttacherType = Attacher::AttachEngine3D
  Height = 44
  Length = 12
  Placement = pos=(28,-2.25,-41) rot=(0,0,1;0rad)
  Width = 31
FEATURE [Part::Cut] Cut207
  Base = -> Box001027045172
  Tool = -> Box001027045173
FEATURE [Part::Cut] Cut208
  Base = -> Cut193
  Tool = -> Cut202
FEATURE [Part::MultiCommon] Common092
  Shapes = -> [Cut206,Cut207]
FEATURE [Part::Box] Box001027045174  label="Cube222"
  AttacherType = Attacher::AttachEngine3D
  Height = 24
  Length = 10
  Placement = pos=(29,-8.5,-34) rot=(0,0,1;0rad)
  Width = 4
FEATURE [Part::Cylinder] Cylinder226  label="M3-clearance001"
  Angle = 360
  AttacherType = Attacher::AttachEngine3D
  Height = 20
  Placement = pos=(34,5,-14) rot=(1,0,0;1.5708rad)
  Radius = 1.7
FEATURE [Part::Cylinder] Cylinder227  label="M3-clearance002"
  Angle = 360
  AttacherType = Attacher::AttachEngine3D
  Height = 20
  Placement = pos=(34,5,-29) rot=(1,0,0;1.5708rad)
  Radius = 1.7
FEATURE [Part::Cylinder] Cylinder228  label="M3-clearance003"
  Angle = 360
  AttacherType = Attacher::AttachEngine3D
  Height = 20
  Placement = pos=(34,5,-14) rot=(1,0,0;1.5708rad)
  Radius = 1.7
FEATURE [Part::Cylinder] Cylinder229  label="M3-clearance004"
  Angle = 360
  AttacherType = Attacher::AttachEngine3D
  Height = 20
  Placement = pos=(34,5,-29) rot=(1,0,0;1.5708rad)
  Radius = 1.7
FEATURE [Part::Cylinder] Cylinder230  label="M3-tap005"
  Angle = 360
  AttacherType = Attacher::AttachEngine3D
  Height = 20
  Placement = pos=(34,5,-14) rot=(1,0,0;1.5708rad)
  Radius = 1.4
FEATURE [Part::Cylinder] Cylinder231  label="M3-tap006"
  Angle = 360
  AttacherType = Attacher::AttachEngine3D
  Height = 20
  Placement = pos=(34,5,-29) rot=(1,0,0;1.5708rad)
  Radius = 1.4
FEATURE [Part::MultiFuse] Fusion112121
  Shapes = -> [Cylinder226,Cylinder227]
FEATURE [Part::MultiFuse] Fusion112122
  Shapes = -> [Cylinder228,Cylinder229]
FEATURE [Part::MultiFuse] Fusion112123
  Shapes = -> [Cylinder230,Cylinder231]
FEATURE [Part::Cut] Cut209  label="join-plate"
  Base = -> Box001027045174
  Tool = -> Fusion112123
FEATURE [Part::Cut] Cut210  label="cutter-arm-1"
  Base = -> Cut208
  Tool = -> Fusion112121
FEATURE [Part::Cut] Cut211  label="cutter-extension-1"
  Base = -> Common092
  Tool = -> Fusion112122
FEATURE [Part::Chamfer] Chamfer021
  Base = -> Cut210
  Edges = 1 edges r=2.2: [Edge107]
FEATURE [Part::Chamfer] Chamfer022
  Base = -> Chamfer021
  Edges = 3 edges r=2.2: [Edge5,Edge20,Edge21]
FEATURE [Part::Chamfer] Chamfer023
  Base = -> Cut211
  Edges = 1 edges r=2: [Edge28]
FEATURE [Part::Cylinder] Cylinder232  label="Cylinder261"
  Angle = 360
  AttacherType = Attacher::AttachEngine3D
  Height = 30
  Placement = pos=(19.5,2,-45) rot=(0,0,1;0rad)
  Radius = 1.4
FEATURE [Part::Box] Box001027045175  label="Cube223"
  AttacherType = Attacher::AttachEngine3D
  Height = 9
  Length = 13
  Placement = pos=(15,-4.5,-34) rot=(0,0,1;0rad)
  Width = 9.5
FEATURE [Part::Chamfer] Chamfer024
  Base = -> Box001027045175
  Edges = 1 edges r=3: [Edge6]
FEATURE [Part::Fillet] Fillet040
  Base = -> Chamfer024
  Edges = 2 edges r=2: [Edge2,Edge9]
FEATURE [Part::MultiFuse] Fusion112124
  Shapes = -> [Chamfer023,Fillet040]
FEATURE [Part::Cut] Cut212
  Base = -> Fusion112124
  Tool = -> Cylinder232
FEATURE [Part::Chamfer] Chamfer025
  Base = -> Cut212
  Edges = 1 edges r=2.5: [Edge30]
FEATURE [Part::Cut] Cut213
  Base = -> Chamfer025
  Tool = -> Fusion112115
FEATURE [Part::Cut] Cut214
  Base = -> Cut213
  Tool = -> Fusion112118
FEATURE [Part::Cylinder] Cylinder233  label="rocker-cut003"
  Angle = 360
  AttacherType = Attacher::AttachEngine3D
  Height = 18
  Placement = pos=(0,9,-8) rot=(1,0,0;1.5708rad)
  Radius = 4.2
FEATURE [Part::Cut] Cut215
  Base = -> Cut214
  Tool = -> Cylinder233
FEATURE [Part::Box] Box001027045176  label="Cube224"
  AttacherType = Attacher::AttachEngine3D
  Height = 10
  Length = 10
  Placement = pos=(-4,-7,-32) rot=(0,0,1;0rad)
  Width = 15
FEATURE [Part::Cut] Cut216
  Base = -> Cut215
  Tool = -> Box001027045176
FEATURE [Part::Fillet] Fillet041  label="cutting-arm"
  Base = -> Chamfer022
  Edges = 2 edges r=10: [Edge49,Edge58]
FEATURE [Part::Fillet] Fillet042  label="cutting-arm-extension"
  Base = -> Cut216
  Edges = 1 edges r=7: [Edge105]
FEATURE [App::DocumentObjectGroup] Group004  label="Moving-arm"
  Group = -> [Fillet032,Cut209,Fillet041,Fillet042]
FEATURE [Part::Chamfer] Chamfer026
  Base = -> Cut189
  Edges = 1 edges r=4: [Edge73]
FEATURE [Part::Chamfer] Chamfer027  label="base-and-mount"
  Base = -> Chamfer026
  Edges = 1 edges r=4: [Edge34]
FEATURE [Part::Chamfer] Chamfer028  label="bearing-support-1"
  Base = -> Fillet038
  Edges = 1 edges r=3.9: [Edge21]
FEATURE [Part::Chamfer] Chamfer029  label="bearing-support-2"
  Base = -> Fillet039
  Edges = 1 edges r=3.9: [Edge5]
FEATURE [App::DocumentObjectGroup] Group005  label="Stationary-arm"
  Group = -> [Chamfer027,Chamfer029,Chamfer028]
